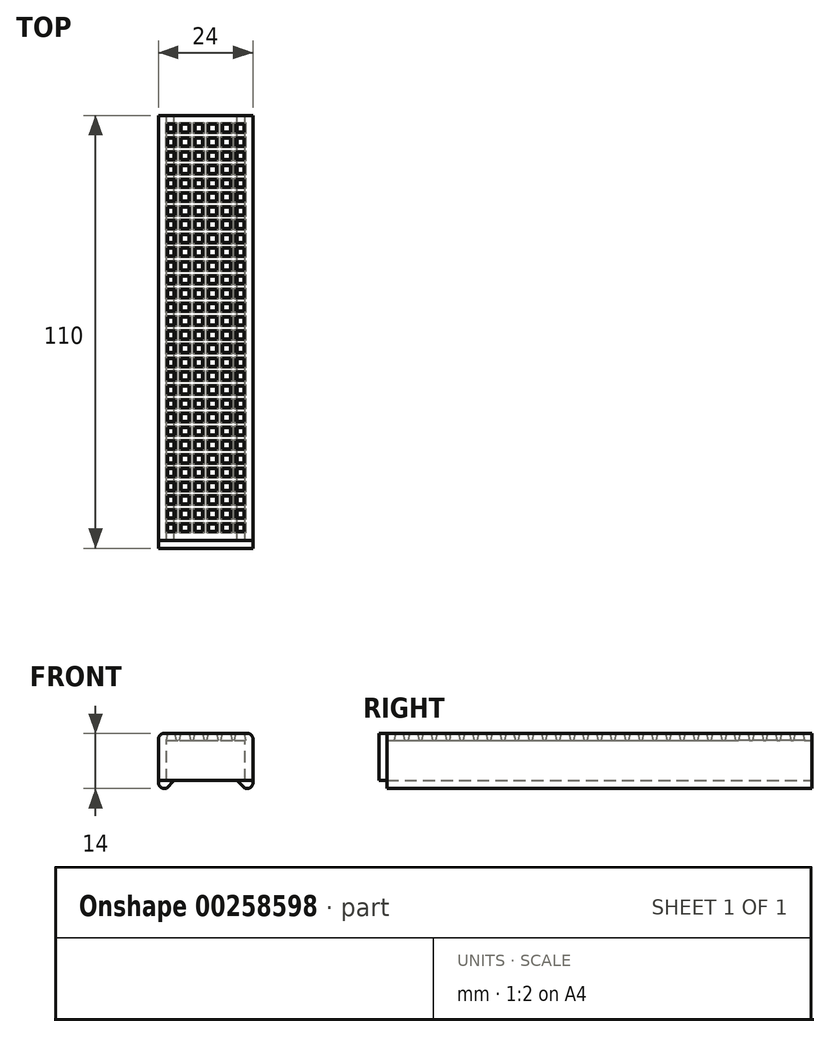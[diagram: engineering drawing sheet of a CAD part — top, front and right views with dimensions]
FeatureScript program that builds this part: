
annotation { "Feature Type Name" : "Feature", "Feature Type Description" : "" }
export const myFeature = defineFeature(function(context is Context, id is Id, definition is map)
    precondition{}
    {
        {
            var Q0;
            Q0=qCreatedBy(makeId("Front.planeOp"),FACE);
            var sketch = newSketch(context, id + "F0", { "sketchPlane" : qUnion([Q0])});
            skLineSegment(sketch, "E0.bottom", {"start": v(-10, -5.1) * mm, "end": v(-8, -5.1) * mm});
            skLineSegment(sketch, "E0.left", {"start": v(-10, -5.1) * mm, "end": v(-10, 5.1) * mm});
            skLineSegment(sketch, "E0.right", {"start": v(10, -5.1) * mm, "end": v(10, 5.1) * mm});
            skPoint(sketch, "E0.middle", {"position": v(0, 0) * mm});
            skPoint(sketch, "E1", {"position": v(-8, -5.1) * mm});
            skPoint(sketch, "E2.MirrorP", {"position": v(8, -5.1) * mm});
            skLineSegment(sketch, "E3", {"start": v(-8, -5.1) * mm, "end": v(-10, -7.1) * mm});
            skLineSegment(sketch, "E4", {"start": v(8, -5.1) * mm, "end": v(10, -7.1) * mm});
            skLineSegment(sketch, "E5", {"start": v(-12, -7.1) * mm, "end": v(-10, -7.1) * mm});
            skLineSegment(sketch, "E6.trimOffspring", {"start": v(10, -7.1) * mm, "end": v(12, -7.1) * mm});
            skLineSegment(sketch, "E7.trimOffspring", {"start": v(8, -5.1) * mm, "end": v(10, -5.1) * mm});
            skLineSegment(sketch, "E8", {"start": v(-10, 5.1) * mm, "end": v(10, 5.1) * mm});
            skLineSegment(sketch, "E9", {"start": v(-12, 6.9) * mm, "end": v(12, 6.9) * mm});
            skLineSegment(sketch, "E10", {"start": v(-12, -7.1) * mm, "end": v(-12, 6.9) * mm});
            skLineSegment(sketch, "E11", {"start": v(12, -7.1) * mm, "end": v(12, 6.9) * mm});
            skSolve(sketch);
        }
        {
            var Q0;
            Q0 = qSketchRegion(id + "F0", true);
            extrude(context, id + "F1", {"entities" : qUnion([Q0]), "depth" : 108 * mm});
        }
        {
            var Q0;
            Q0=makeQuery(id+"F1.opExtrude","SWEPT_FACE",FACE,{"disambiguationData":[OSD([sQuery(id+"F0.wireOp",EDGE,"E9")])]});
            var sketch = newSketch(context, id + "F2", { "sketchPlane" : qUnion([Q0])});
            skLineSegment(sketch, "E12.bottom", {"start": v(-9.75, -105.75) * mm, "end": v(-7.75, -105.75) * mm});
            skLineSegment(sketch, "E12.top", {"start": v(-9.75, -103.75) * mm, "end": v(-7.75, -103.75) * mm});
            skLineSegment(sketch, "E12.left", {"start": v(-9.75, -105.75) * mm, "end": v(-9.75, -103.75) * mm});
            skLineSegment(sketch, "E12.right", {"start": v(-7.75, -105.75) * mm, "end": v(-7.75, -103.75) * mm});
            skLineSegment(sketch, "E13.0.1.0", {"start": v(-7.75, -102.25) * mm, "end": v(-7.75, -100.25) * mm});
            skLineSegment(sketch, "E13.0.1.1", {"start": v(-9.75, -102.25) * mm, "end": v(-9.75, -100.25) * mm});
            skLineSegment(sketch, "E13.0.1.2", {"start": v(-9.75, -100.25) * mm, "end": v(-7.75, -100.25) * mm});
            skLineSegment(sketch, "E13.0.1.3", {"start": v(-9.75, -102.25) * mm, "end": v(-7.75, -102.25) * mm});
            skLineSegment(sketch, "E13.0.2.0", {"start": v(-7.75, -98.75) * mm, "end": v(-7.75, -96.75) * mm});
            skLineSegment(sketch, "E13.0.2.1", {"start": v(-9.75, -98.75) * mm, "end": v(-9.75, -96.75) * mm});
            skLineSegment(sketch, "E13.0.2.2", {"start": v(-9.75, -96.75) * mm, "end": v(-7.75, -96.75) * mm});
            skLineSegment(sketch, "E13.0.2.3", {"start": v(-9.75, -98.75) * mm, "end": v(-7.75, -98.75) * mm});
            skLineSegment(sketch, "E13.0.3.0", {"start": v(-7.75, -95.25) * mm, "end": v(-7.75, -93.25) * mm});
            skLineSegment(sketch, "E13.0.3.1", {"start": v(-9.75, -95.25) * mm, "end": v(-9.75, -93.25) * mm});
            skLineSegment(sketch, "E13.0.3.2", {"start": v(-9.75, -93.25) * mm, "end": v(-7.75, -93.25) * mm});
            skLineSegment(sketch, "E13.0.3.3", {"start": v(-9.75, -95.25) * mm, "end": v(-7.75, -95.25) * mm});
            skLineSegment(sketch, "E13.0.4.0", {"start": v(-7.75, -91.75) * mm, "end": v(-7.75, -89.75) * mm});
            skLineSegment(sketch, "E13.0.4.1", {"start": v(-9.75, -91.75) * mm, "end": v(-9.75, -89.75) * mm});
            skLineSegment(sketch, "E13.0.4.2", {"start": v(-9.75, -89.75) * mm, "end": v(-7.75, -89.75) * mm});
            skLineSegment(sketch, "E13.0.4.3", {"start": v(-9.75, -91.75) * mm, "end": v(-7.75, -91.75) * mm});
            skLineSegment(sketch, "E13.0.5.0", {"start": v(-7.75, -88.25) * mm, "end": v(-7.75, -86.25) * mm});
            skLineSegment(sketch, "E13.0.5.1", {"start": v(-9.75, -88.25) * mm, "end": v(-9.75, -86.25) * mm});
            skLineSegment(sketch, "E13.0.5.2", {"start": v(-9.75, -86.25) * mm, "end": v(-7.75, -86.25) * mm});
            skLineSegment(sketch, "E13.0.5.3", {"start": v(-9.75, -88.25) * mm, "end": v(-7.75, -88.25) * mm});
            skLineSegment(sketch, "E13.0.6.0", {"start": v(-7.75, -84.75) * mm, "end": v(-7.75, -82.75) * mm});
            skLineSegment(sketch, "E13.0.6.1", {"start": v(-9.75, -84.75) * mm, "end": v(-9.75, -82.75) * mm});
            skLineSegment(sketch, "E13.0.6.2", {"start": v(-9.75, -82.75) * mm, "end": v(-7.75, -82.75) * mm});
            skLineSegment(sketch, "E13.0.6.3", {"start": v(-9.75, -84.75) * mm, "end": v(-7.75, -84.75) * mm});
            skLineSegment(sketch, "E13.0.7.0", {"start": v(-7.75, -81.25) * mm, "end": v(-7.75, -79.25) * mm});
            skLineSegment(sketch, "E13.0.7.1", {"start": v(-9.75, -81.25) * mm, "end": v(-9.75, -79.25) * mm});
            skLineSegment(sketch, "E13.0.7.2", {"start": v(-9.75, -79.25) * mm, "end": v(-7.75, -79.25) * mm});
            skLineSegment(sketch, "E13.0.7.3", {"start": v(-9.75, -81.25) * mm, "end": v(-7.75, -81.25) * mm});
            skLineSegment(sketch, "E13.0.8.0", {"start": v(-7.75, -77.75) * mm, "end": v(-7.75, -75.75) * mm});
            skLineSegment(sketch, "E13.0.8.1", {"start": v(-9.75, -77.75) * mm, "end": v(-9.75, -75.75) * mm});
            skLineSegment(sketch, "E13.0.8.2", {"start": v(-9.75, -75.75) * mm, "end": v(-7.75, -75.75) * mm});
            skLineSegment(sketch, "E13.0.8.3", {"start": v(-9.75, -77.75) * mm, "end": v(-7.75, -77.75) * mm});
            skLineSegment(sketch, "E13.0.9.0", {"start": v(-7.75, -74.25) * mm, "end": v(-7.75, -72.25) * mm});
            skLineSegment(sketch, "E13.0.9.1", {"start": v(-9.75, -74.25) * mm, "end": v(-9.75, -72.25) * mm});
            skLineSegment(sketch, "E13.0.9.2", {"start": v(-9.75, -72.25) * mm, "end": v(-7.75, -72.25) * mm});
            skLineSegment(sketch, "E13.0.9.3", {"start": v(-9.75, -74.25) * mm, "end": v(-7.75, -74.25) * mm});
            skLineSegment(sketch, "E13.0.10.0", {"start": v(-7.75, -70.75) * mm, "end": v(-7.75, -68.75) * mm});
            skLineSegment(sketch, "E13.0.10.1", {"start": v(-9.75, -70.75) * mm, "end": v(-9.75, -68.75) * mm});
            skLineSegment(sketch, "E13.0.10.2", {"start": v(-9.75, -68.75) * mm, "end": v(-7.75, -68.75) * mm});
            skLineSegment(sketch, "E13.0.10.3", {"start": v(-9.75, -70.75) * mm, "end": v(-7.75, -70.75) * mm});
            skLineSegment(sketch, "E13.0.11.0", {"start": v(-7.75, -67.25) * mm, "end": v(-7.75, -65.25) * mm});
            skLineSegment(sketch, "E13.0.11.1", {"start": v(-9.75, -67.25) * mm, "end": v(-9.75, -65.25) * mm});
            skLineSegment(sketch, "E13.0.11.2", {"start": v(-9.75, -65.25) * mm, "end": v(-7.75, -65.25) * mm});
            skLineSegment(sketch, "E13.0.11.3", {"start": v(-9.75, -67.25) * mm, "end": v(-7.75, -67.25) * mm});
            skLineSegment(sketch, "E13.0.12.0", {"start": v(-7.75, -63.75) * mm, "end": v(-7.75, -61.75) * mm});
            skLineSegment(sketch, "E13.0.12.1", {"start": v(-9.75, -63.75) * mm, "end": v(-9.75, -61.75) * mm});
            skLineSegment(sketch, "E13.0.12.2", {"start": v(-9.75, -61.75) * mm, "end": v(-7.75, -61.75) * mm});
            skLineSegment(sketch, "E13.0.12.3", {"start": v(-9.75, -63.75) * mm, "end": v(-7.75, -63.75) * mm});
            skLineSegment(sketch, "E13.0.13.0", {"start": v(-7.75, -60.25) * mm, "end": v(-7.75, -58.25) * mm});
            skLineSegment(sketch, "E13.0.13.1", {"start": v(-9.75, -60.25) * mm, "end": v(-9.75, -58.25) * mm});
            skLineSegment(sketch, "E13.0.13.2", {"start": v(-9.75, -58.25) * mm, "end": v(-7.75, -58.25) * mm});
            skLineSegment(sketch, "E13.0.13.3", {"start": v(-9.75, -60.25) * mm, "end": v(-7.75, -60.25) * mm});
            skLineSegment(sketch, "E13.0.14.0", {"start": v(-7.75, -56.75) * mm, "end": v(-7.75, -54.75) * mm});
            skLineSegment(sketch, "E13.0.14.1", {"start": v(-9.75, -56.75) * mm, "end": v(-9.75, -54.75) * mm});
            skLineSegment(sketch, "E13.0.14.2", {"start": v(-9.75, -54.75) * mm, "end": v(-7.75, -54.75) * mm});
            skLineSegment(sketch, "E13.0.14.3", {"start": v(-9.75, -56.75) * mm, "end": v(-7.75, -56.75) * mm});
            skLineSegment(sketch, "E13.0.15.0", {"start": v(-7.75, -53.25) * mm, "end": v(-7.75, -51.25) * mm});
            skLineSegment(sketch, "E13.0.15.1", {"start": v(-9.75, -53.25) * mm, "end": v(-9.75, -51.25) * mm});
            skLineSegment(sketch, "E13.0.15.2", {"start": v(-9.75, -51.25) * mm, "end": v(-7.75, -51.25) * mm});
            skLineSegment(sketch, "E13.0.15.3", {"start": v(-9.75, -53.25) * mm, "end": v(-7.75, -53.25) * mm});
            skLineSegment(sketch, "E13.0.16.0", {"start": v(-7.75, -49.75) * mm, "end": v(-7.75, -47.75) * mm});
            skLineSegment(sketch, "E13.0.16.1", {"start": v(-9.75, -49.75) * mm, "end": v(-9.75, -47.75) * mm});
            skLineSegment(sketch, "E13.0.16.2", {"start": v(-9.75, -47.75) * mm, "end": v(-7.75, -47.75) * mm});
            skLineSegment(sketch, "E13.0.16.3", {"start": v(-9.75, -49.75) * mm, "end": v(-7.75, -49.75) * mm});
            skLineSegment(sketch, "E13.0.17.0", {"start": v(-7.75, -46.25) * mm, "end": v(-7.75, -44.25) * mm});
            skLineSegment(sketch, "E13.0.17.1", {"start": v(-9.75, -46.25) * mm, "end": v(-9.75, -44.25) * mm});
            skLineSegment(sketch, "E13.0.17.2", {"start": v(-9.75, -44.25) * mm, "end": v(-7.75, -44.25) * mm});
            skLineSegment(sketch, "E13.0.17.3", {"start": v(-9.75, -46.25) * mm, "end": v(-7.75, -46.25) * mm});
            skLineSegment(sketch, "E13.0.18.0", {"start": v(-7.75, -42.75) * mm, "end": v(-7.75, -40.75) * mm});
            skLineSegment(sketch, "E13.0.18.1", {"start": v(-9.75, -42.75) * mm, "end": v(-9.75, -40.75) * mm});
            skLineSegment(sketch, "E13.0.18.2", {"start": v(-9.75, -40.75) * mm, "end": v(-7.75, -40.75) * mm});
            skLineSegment(sketch, "E13.0.18.3", {"start": v(-9.75, -42.75) * mm, "end": v(-7.75, -42.75) * mm});
            skLineSegment(sketch, "E13.0.19.0", {"start": v(-7.75, -39.25) * mm, "end": v(-7.75, -37.25) * mm});
            skLineSegment(sketch, "E13.0.19.1", {"start": v(-9.75, -39.25) * mm, "end": v(-9.75, -37.25) * mm});
            skLineSegment(sketch, "E13.0.19.2", {"start": v(-9.75, -37.25) * mm, "end": v(-7.75, -37.25) * mm});
            skLineSegment(sketch, "E13.0.19.3", {"start": v(-9.75, -39.25) * mm, "end": v(-7.75, -39.25) * mm});
            skLineSegment(sketch, "E13.0.20.0", {"start": v(-7.75, -35.75) * mm, "end": v(-7.75, -33.75) * mm});
            skLineSegment(sketch, "E13.0.20.1", {"start": v(-9.75, -35.75) * mm, "end": v(-9.75, -33.75) * mm});
            skLineSegment(sketch, "E13.0.20.2", {"start": v(-9.75, -33.75) * mm, "end": v(-7.75, -33.75) * mm});
            skLineSegment(sketch, "E13.0.20.3", {"start": v(-9.75, -35.75) * mm, "end": v(-7.75, -35.75) * mm});
            skLineSegment(sketch, "E13.0.21.0", {"start": v(-7.75, -32.25) * mm, "end": v(-7.75, -30.25) * mm});
            skLineSegment(sketch, "E13.0.21.1", {"start": v(-9.75, -32.25) * mm, "end": v(-9.75, -30.25) * mm});
            skLineSegment(sketch, "E13.0.21.2", {"start": v(-9.75, -30.25) * mm, "end": v(-7.75, -30.25) * mm});
            skLineSegment(sketch, "E13.0.21.3", {"start": v(-9.75, -32.25) * mm, "end": v(-7.75, -32.25) * mm});
            skLineSegment(sketch, "E13.0.22.0", {"start": v(-7.75, -28.75) * mm, "end": v(-7.75, -26.75) * mm});
            skLineSegment(sketch, "E13.0.22.1", {"start": v(-9.75, -28.75) * mm, "end": v(-9.75, -26.75) * mm});
            skLineSegment(sketch, "E13.0.22.2", {"start": v(-9.75, -26.75) * mm, "end": v(-7.75, -26.75) * mm});
            skLineSegment(sketch, "E13.0.22.3", {"start": v(-9.75, -28.75) * mm, "end": v(-7.75, -28.75) * mm});
            skLineSegment(sketch, "E13.0.23.0", {"start": v(-7.75, -25.25) * mm, "end": v(-7.75, -23.25) * mm});
            skLineSegment(sketch, "E13.0.23.1", {"start": v(-9.75, -25.25) * mm, "end": v(-9.75, -23.25) * mm});
            skLineSegment(sketch, "E13.0.23.2", {"start": v(-9.75, -23.25) * mm, "end": v(-7.75, -23.25) * mm});
            skLineSegment(sketch, "E13.0.23.3", {"start": v(-9.75, -25.25) * mm, "end": v(-7.75, -25.25) * mm});
            skLineSegment(sketch, "E13.0.24.0", {"start": v(-7.75, -21.75) * mm, "end": v(-7.75, -19.75) * mm});
            skLineSegment(sketch, "E13.0.24.1", {"start": v(-9.75, -21.75) * mm, "end": v(-9.75, -19.75) * mm});
            skLineSegment(sketch, "E13.0.24.2", {"start": v(-9.75, -19.75) * mm, "end": v(-7.75, -19.75) * mm});
            skLineSegment(sketch, "E13.0.24.3", {"start": v(-9.75, -21.75) * mm, "end": v(-7.75, -21.75) * mm});
            skLineSegment(sketch, "E13.1.0.0", {"start": v(-4.25, -105.75) * mm, "end": v(-4.25, -103.75) * mm});
            skLineSegment(sketch, "E13.1.0.1", {"start": v(-6.25, -105.75) * mm, "end": v(-6.25, -103.75) * mm});
            skLineSegment(sketch, "E13.1.0.2", {"start": v(-6.25, -103.75) * mm, "end": v(-4.25, -103.75) * mm});
            skLineSegment(sketch, "E13.1.0.3", {"start": v(-6.25, -105.75) * mm, "end": v(-4.25, -105.75) * mm});
            skLineSegment(sketch, "E13.1.1.0", {"start": v(-4.25, -102.25) * mm, "end": v(-4.25, -100.25) * mm});
            skLineSegment(sketch, "E13.1.1.1", {"start": v(-6.25, -102.25) * mm, "end": v(-6.25, -100.25) * mm});
            skLineSegment(sketch, "E13.1.1.2", {"start": v(-6.25, -100.25) * mm, "end": v(-4.25, -100.25) * mm});
            skLineSegment(sketch, "E13.1.1.3", {"start": v(-6.25, -102.25) * mm, "end": v(-4.25, -102.25) * mm});
            skLineSegment(sketch, "E13.1.2.0", {"start": v(-4.25, -98.75) * mm, "end": v(-4.25, -96.75) * mm});
            skLineSegment(sketch, "E13.1.2.1", {"start": v(-6.25, -98.75) * mm, "end": v(-6.25, -96.75) * mm});
            skLineSegment(sketch, "E13.1.2.2", {"start": v(-6.25, -96.75) * mm, "end": v(-4.25, -96.75) * mm});
            skLineSegment(sketch, "E13.1.2.3", {"start": v(-6.25, -98.75) * mm, "end": v(-4.25, -98.75) * mm});
            skLineSegment(sketch, "E13.1.3.0", {"start": v(-4.25, -95.25) * mm, "end": v(-4.25, -93.25) * mm});
            skLineSegment(sketch, "E13.1.3.1", {"start": v(-6.25, -95.25) * mm, "end": v(-6.25, -93.25) * mm});
            skLineSegment(sketch, "E13.1.3.2", {"start": v(-6.25, -93.25) * mm, "end": v(-4.25, -93.25) * mm});
            skLineSegment(sketch, "E13.1.3.3", {"start": v(-6.25, -95.25) * mm, "end": v(-4.25, -95.25) * mm});
            skLineSegment(sketch, "E13.1.4.0", {"start": v(-4.25, -91.75) * mm, "end": v(-4.25, -89.75) * mm});
            skLineSegment(sketch, "E13.1.4.1", {"start": v(-6.25, -91.75) * mm, "end": v(-6.25, -89.75) * mm});
            skLineSegment(sketch, "E13.1.4.2", {"start": v(-6.25, -89.75) * mm, "end": v(-4.25, -89.75) * mm});
            skLineSegment(sketch, "E13.1.4.3", {"start": v(-6.25, -91.75) * mm, "end": v(-4.25, -91.75) * mm});
            skLineSegment(sketch, "E13.1.5.0", {"start": v(-4.25, -88.25) * mm, "end": v(-4.25, -86.25) * mm});
            skLineSegment(sketch, "E13.1.5.1", {"start": v(-6.25, -88.25) * mm, "end": v(-6.25, -86.25) * mm});
            skLineSegment(sketch, "E13.1.5.2", {"start": v(-6.25, -86.25) * mm, "end": v(-4.25, -86.25) * mm});
            skLineSegment(sketch, "E13.1.5.3", {"start": v(-6.25, -88.25) * mm, "end": v(-4.25, -88.25) * mm});
            skLineSegment(sketch, "E13.1.6.0", {"start": v(-4.25, -84.75) * mm, "end": v(-4.25, -82.75) * mm});
            skLineSegment(sketch, "E13.1.6.1", {"start": v(-6.25, -84.75) * mm, "end": v(-6.25, -82.75) * mm});
            skLineSegment(sketch, "E13.1.6.2", {"start": v(-6.25, -82.75) * mm, "end": v(-4.25, -82.75) * mm});
            skLineSegment(sketch, "E13.1.6.3", {"start": v(-6.25, -84.75) * mm, "end": v(-4.25, -84.75) * mm});
            skLineSegment(sketch, "E13.1.7.0", {"start": v(-4.25, -81.25) * mm, "end": v(-4.25, -79.25) * mm});
            skLineSegment(sketch, "E13.1.7.1", {"start": v(-6.25, -81.25) * mm, "end": v(-6.25, -79.25) * mm});
            skLineSegment(sketch, "E13.1.7.2", {"start": v(-6.25, -79.25) * mm, "end": v(-4.25, -79.25) * mm});
            skLineSegment(sketch, "E13.1.7.3", {"start": v(-6.25, -81.25) * mm, "end": v(-4.25, -81.25) * mm});
            skLineSegment(sketch, "E13.1.8.0", {"start": v(-4.25, -77.75) * mm, "end": v(-4.25, -75.75) * mm});
            skLineSegment(sketch, "E13.1.8.1", {"start": v(-6.25, -77.75) * mm, "end": v(-6.25, -75.75) * mm});
            skLineSegment(sketch, "E13.1.8.2", {"start": v(-6.25, -75.75) * mm, "end": v(-4.25, -75.75) * mm});
            skLineSegment(sketch, "E13.1.8.3", {"start": v(-6.25, -77.75) * mm, "end": v(-4.25, -77.75) * mm});
            skLineSegment(sketch, "E13.1.9.0", {"start": v(-4.25, -74.25) * mm, "end": v(-4.25, -72.25) * mm});
            skLineSegment(sketch, "E13.1.9.1", {"start": v(-6.25, -74.25) * mm, "end": v(-6.25, -72.25) * mm});
            skLineSegment(sketch, "E13.1.9.2", {"start": v(-6.25, -72.25) * mm, "end": v(-4.25, -72.25) * mm});
            skLineSegment(sketch, "E13.1.9.3", {"start": v(-6.25, -74.25) * mm, "end": v(-4.25, -74.25) * mm});
            skLineSegment(sketch, "E13.1.10.0", {"start": v(-4.25, -70.75) * mm, "end": v(-4.25, -68.75) * mm});
            skLineSegment(sketch, "E13.1.10.1", {"start": v(-6.25, -70.75) * mm, "end": v(-6.25, -68.75) * mm});
            skLineSegment(sketch, "E13.1.10.2", {"start": v(-6.25, -68.75) * mm, "end": v(-4.25, -68.75) * mm});
            skLineSegment(sketch, "E13.1.10.3", {"start": v(-6.25, -70.75) * mm, "end": v(-4.25, -70.75) * mm});
            skLineSegment(sketch, "E13.1.11.0", {"start": v(-4.25, -67.25) * mm, "end": v(-4.25, -65.25) * mm});
            skLineSegment(sketch, "E13.1.11.1", {"start": v(-6.25, -67.25) * mm, "end": v(-6.25, -65.25) * mm});
            skLineSegment(sketch, "E13.1.11.2", {"start": v(-6.25, -65.25) * mm, "end": v(-4.25, -65.25) * mm});
            skLineSegment(sketch, "E13.1.11.3", {"start": v(-6.25, -67.25) * mm, "end": v(-4.25, -67.25) * mm});
            skLineSegment(sketch, "E13.1.12.0", {"start": v(-4.25, -63.75) * mm, "end": v(-4.25, -61.75) * mm});
            skLineSegment(sketch, "E13.1.12.1", {"start": v(-6.25, -63.75) * mm, "end": v(-6.25, -61.75) * mm});
            skLineSegment(sketch, "E13.1.12.2", {"start": v(-6.25, -61.75) * mm, "end": v(-4.25, -61.75) * mm});
            skLineSegment(sketch, "E13.1.12.3", {"start": v(-6.25, -63.75) * mm, "end": v(-4.25, -63.75) * mm});
            skLineSegment(sketch, "E13.1.13.0", {"start": v(-4.25, -60.25) * mm, "end": v(-4.25, -58.25) * mm});
            skLineSegment(sketch, "E13.1.13.1", {"start": v(-6.25, -60.25) * mm, "end": v(-6.25, -58.25) * mm});
            skLineSegment(sketch, "E13.1.13.2", {"start": v(-6.25, -58.25) * mm, "end": v(-4.25, -58.25) * mm});
            skLineSegment(sketch, "E13.1.13.3", {"start": v(-6.25, -60.25) * mm, "end": v(-4.25, -60.25) * mm});
            skLineSegment(sketch, "E13.1.14.0", {"start": v(-4.25, -56.75) * mm, "end": v(-4.25, -54.75) * mm});
            skLineSegment(sketch, "E13.1.14.1", {"start": v(-6.25, -56.75) * mm, "end": v(-6.25, -54.75) * mm});
            skLineSegment(sketch, "E13.1.14.2", {"start": v(-6.25, -54.75) * mm, "end": v(-4.25, -54.75) * mm});
            skLineSegment(sketch, "E13.1.14.3", {"start": v(-6.25, -56.75) * mm, "end": v(-4.25, -56.75) * mm});
            skLineSegment(sketch, "E13.1.15.0", {"start": v(-4.25, -53.25) * mm, "end": v(-4.25, -51.25) * mm});
            skLineSegment(sketch, "E13.1.15.1", {"start": v(-6.25, -53.25) * mm, "end": v(-6.25, -51.25) * mm});
            skLineSegment(sketch, "E13.1.15.2", {"start": v(-6.25, -51.25) * mm, "end": v(-4.25, -51.25) * mm});
            skLineSegment(sketch, "E13.1.15.3", {"start": v(-6.25, -53.25) * mm, "end": v(-4.25, -53.25) * mm});
            skLineSegment(sketch, "E13.1.16.0", {"start": v(-4.25, -49.75) * mm, "end": v(-4.25, -47.75) * mm});
            skLineSegment(sketch, "E13.1.16.1", {"start": v(-6.25, -49.75) * mm, "end": v(-6.25, -47.75) * mm});
            skLineSegment(sketch, "E13.1.16.2", {"start": v(-6.25, -47.75) * mm, "end": v(-4.25, -47.75) * mm});
            skLineSegment(sketch, "E13.1.16.3", {"start": v(-6.25, -49.75) * mm, "end": v(-4.25, -49.75) * mm});
            skLineSegment(sketch, "E13.1.17.0", {"start": v(-4.25, -46.25) * mm, "end": v(-4.25, -44.25) * mm});
            skLineSegment(sketch, "E13.1.17.1", {"start": v(-6.25, -46.25) * mm, "end": v(-6.25, -44.25) * mm});
            skLineSegment(sketch, "E13.1.17.2", {"start": v(-6.25, -44.25) * mm, "end": v(-4.25, -44.25) * mm});
            skLineSegment(sketch, "E13.1.17.3", {"start": v(-6.25, -46.25) * mm, "end": v(-4.25, -46.25) * mm});
            skLineSegment(sketch, "E13.1.18.0", {"start": v(-4.25, -42.75) * mm, "end": v(-4.25, -40.75) * mm});
            skLineSegment(sketch, "E13.1.18.1", {"start": v(-6.25, -42.75) * mm, "end": v(-6.25, -40.75) * mm});
            skLineSegment(sketch, "E13.1.18.2", {"start": v(-6.25, -40.75) * mm, "end": v(-4.25, -40.75) * mm});
            skLineSegment(sketch, "E13.1.18.3", {"start": v(-6.25, -42.75) * mm, "end": v(-4.25, -42.75) * mm});
            skLineSegment(sketch, "E13.1.19.0", {"start": v(-4.25, -39.25) * mm, "end": v(-4.25, -37.25) * mm});
            skLineSegment(sketch, "E13.1.19.1", {"start": v(-6.25, -39.25) * mm, "end": v(-6.25, -37.25) * mm});
            skLineSegment(sketch, "E13.1.19.2", {"start": v(-6.25, -37.25) * mm, "end": v(-4.25, -37.25) * mm});
            skLineSegment(sketch, "E13.1.19.3", {"start": v(-6.25, -39.25) * mm, "end": v(-4.25, -39.25) * mm});
            skLineSegment(sketch, "E13.1.20.0", {"start": v(-4.25, -35.75) * mm, "end": v(-4.25, -33.75) * mm});
            skLineSegment(sketch, "E13.1.20.1", {"start": v(-6.25, -35.75) * mm, "end": v(-6.25, -33.75) * mm});
            skLineSegment(sketch, "E13.1.20.2", {"start": v(-6.25, -33.75) * mm, "end": v(-4.25, -33.75) * mm});
            skLineSegment(sketch, "E13.1.20.3", {"start": v(-6.25, -35.75) * mm, "end": v(-4.25, -35.75) * mm});
            skLineSegment(sketch, "E13.1.21.0", {"start": v(-4.25, -32.25) * mm, "end": v(-4.25, -30.25) * mm});
            skLineSegment(sketch, "E13.1.21.1", {"start": v(-6.25, -32.25) * mm, "end": v(-6.25, -30.25) * mm});
            skLineSegment(sketch, "E13.1.21.2", {"start": v(-6.25, -30.25) * mm, "end": v(-4.25, -30.25) * mm});
            skLineSegment(sketch, "E13.1.21.3", {"start": v(-6.25, -32.25) * mm, "end": v(-4.25, -32.25) * mm});
            skLineSegment(sketch, "E13.1.22.0", {"start": v(-4.25, -28.75) * mm, "end": v(-4.25, -26.75) * mm});
            skLineSegment(sketch, "E13.1.22.1", {"start": v(-6.25, -28.75) * mm, "end": v(-6.25, -26.75) * mm});
            skLineSegment(sketch, "E13.1.22.2", {"start": v(-6.25, -26.75) * mm, "end": v(-4.25, -26.75) * mm});
            skLineSegment(sketch, "E13.1.22.3", {"start": v(-6.25, -28.75) * mm, "end": v(-4.25, -28.75) * mm});
            skLineSegment(sketch, "E13.1.23.0", {"start": v(-4.25, -25.25) * mm, "end": v(-4.25, -23.25) * mm});
            skLineSegment(sketch, "E13.1.23.1", {"start": v(-6.25, -25.25) * mm, "end": v(-6.25, -23.25) * mm});
            skLineSegment(sketch, "E13.1.23.2", {"start": v(-6.25, -23.25) * mm, "end": v(-4.25, -23.25) * mm});
            skLineSegment(sketch, "E13.1.23.3", {"start": v(-6.25, -25.25) * mm, "end": v(-4.25, -25.25) * mm});
            skLineSegment(sketch, "E13.1.24.0", {"start": v(-4.25, -21.75) * mm, "end": v(-4.25, -19.75) * mm});
            skLineSegment(sketch, "E13.1.24.1", {"start": v(-6.25, -21.75) * mm, "end": v(-6.25, -19.75) * mm});
            skLineSegment(sketch, "E13.1.24.2", {"start": v(-6.25, -19.75) * mm, "end": v(-4.25, -19.75) * mm});
            skLineSegment(sketch, "E13.1.24.3", {"start": v(-6.25, -21.75) * mm, "end": v(-4.25, -21.75) * mm});
            skLineSegment(sketch, "E13.2.0.0", {"start": v(-0.75, -105.75) * mm, "end": v(-0.75, -103.75) * mm});
            skLineSegment(sketch, "E13.2.0.1", {"start": v(-2.75, -105.75) * mm, "end": v(-2.75, -103.75) * mm});
            skLineSegment(sketch, "E13.2.0.2", {"start": v(-2.75, -103.75) * mm, "end": v(-0.75, -103.75) * mm});
            skLineSegment(sketch, "E13.2.0.3", {"start": v(-2.75, -105.75) * mm, "end": v(-0.75, -105.75) * mm});
            skLineSegment(sketch, "E13.2.1.0", {"start": v(-0.75, -102.25) * mm, "end": v(-0.75, -100.25) * mm});
            skLineSegment(sketch, "E13.2.1.1", {"start": v(-2.75, -102.25) * mm, "end": v(-2.75, -100.25) * mm});
            skLineSegment(sketch, "E13.2.1.2", {"start": v(-2.75, -100.25) * mm, "end": v(-0.75, -100.25) * mm});
            skLineSegment(sketch, "E13.2.1.3", {"start": v(-2.75, -102.25) * mm, "end": v(-0.75, -102.25) * mm});
            skLineSegment(sketch, "E13.2.2.0", {"start": v(-0.75, -98.75) * mm, "end": v(-0.75, -96.75) * mm});
            skLineSegment(sketch, "E13.2.2.1", {"start": v(-2.75, -98.75) * mm, "end": v(-2.75, -96.75) * mm});
            skLineSegment(sketch, "E13.2.2.2", {"start": v(-2.75, -96.75) * mm, "end": v(-0.75, -96.75) * mm});
            skLineSegment(sketch, "E13.2.2.3", {"start": v(-2.75, -98.75) * mm, "end": v(-0.75, -98.75) * mm});
            skLineSegment(sketch, "E13.2.3.0", {"start": v(-0.75, -95.25) * mm, "end": v(-0.75, -93.25) * mm});
            skLineSegment(sketch, "E13.2.3.1", {"start": v(-2.75, -95.25) * mm, "end": v(-2.75, -93.25) * mm});
            skLineSegment(sketch, "E13.2.3.2", {"start": v(-2.75, -93.25) * mm, "end": v(-0.75, -93.25) * mm});
            skLineSegment(sketch, "E13.2.3.3", {"start": v(-2.75, -95.25) * mm, "end": v(-0.75, -95.25) * mm});
            skLineSegment(sketch, "E13.2.4.0", {"start": v(-0.75, -91.75) * mm, "end": v(-0.75, -89.75) * mm});
            skLineSegment(sketch, "E13.2.4.1", {"start": v(-2.75, -91.75) * mm, "end": v(-2.75, -89.75) * mm});
            skLineSegment(sketch, "E13.2.4.2", {"start": v(-2.75, -89.75) * mm, "end": v(-0.75, -89.75) * mm});
            skLineSegment(sketch, "E13.2.4.3", {"start": v(-2.75, -91.75) * mm, "end": v(-0.75, -91.75) * mm});
            skLineSegment(sketch, "E13.2.5.0", {"start": v(-0.75, -88.25) * mm, "end": v(-0.75, -86.25) * mm});
            skLineSegment(sketch, "E13.2.5.1", {"start": v(-2.75, -88.25) * mm, "end": v(-2.75, -86.25) * mm});
            skLineSegment(sketch, "E13.2.5.2", {"start": v(-2.75, -86.25) * mm, "end": v(-0.75, -86.25) * mm});
            skLineSegment(sketch, "E13.2.5.3", {"start": v(-2.75, -88.25) * mm, "end": v(-0.75, -88.25) * mm});
            skLineSegment(sketch, "E13.2.6.0", {"start": v(-0.75, -84.75) * mm, "end": v(-0.75, -82.75) * mm});
            skLineSegment(sketch, "E13.2.6.1", {"start": v(-2.75, -84.75) * mm, "end": v(-2.75, -82.75) * mm});
            skLineSegment(sketch, "E13.2.6.2", {"start": v(-2.75, -82.75) * mm, "end": v(-0.75, -82.75) * mm});
            skLineSegment(sketch, "E13.2.6.3", {"start": v(-2.75, -84.75) * mm, "end": v(-0.75, -84.75) * mm});
            skLineSegment(sketch, "E13.2.7.0", {"start": v(-0.75, -81.25) * mm, "end": v(-0.75, -79.25) * mm});
            skLineSegment(sketch, "E13.2.7.1", {"start": v(-2.75, -81.25) * mm, "end": v(-2.75, -79.25) * mm});
            skLineSegment(sketch, "E13.2.7.2", {"start": v(-2.75, -79.25) * mm, "end": v(-0.75, -79.25) * mm});
            skLineSegment(sketch, "E13.2.7.3", {"start": v(-2.75, -81.25) * mm, "end": v(-0.75, -81.25) * mm});
            skLineSegment(sketch, "E13.2.8.0", {"start": v(-0.75, -77.75) * mm, "end": v(-0.75, -75.75) * mm});
            skLineSegment(sketch, "E13.2.8.1", {"start": v(-2.75, -77.75) * mm, "end": v(-2.75, -75.75) * mm});
            skLineSegment(sketch, "E13.2.8.2", {"start": v(-2.75, -75.75) * mm, "end": v(-0.75, -75.75) * mm});
            skLineSegment(sketch, "E13.2.8.3", {"start": v(-2.75, -77.75) * mm, "end": v(-0.75, -77.75) * mm});
            skLineSegment(sketch, "E13.2.9.0", {"start": v(-0.75, -74.25) * mm, "end": v(-0.75, -72.25) * mm});
            skLineSegment(sketch, "E13.2.9.1", {"start": v(-2.75, -74.25) * mm, "end": v(-2.75, -72.25) * mm});
            skLineSegment(sketch, "E13.2.9.2", {"start": v(-2.75, -72.25) * mm, "end": v(-0.75, -72.25) * mm});
            skLineSegment(sketch, "E13.2.9.3", {"start": v(-2.75, -74.25) * mm, "end": v(-0.75, -74.25) * mm});
            skLineSegment(sketch, "E13.2.10.0", {"start": v(-0.75, -70.75) * mm, "end": v(-0.75, -68.75) * mm});
            skLineSegment(sketch, "E13.2.10.1", {"start": v(-2.75, -70.75) * mm, "end": v(-2.75, -68.75) * mm});
            skLineSegment(sketch, "E13.2.10.2", {"start": v(-2.75, -68.75) * mm, "end": v(-0.75, -68.75) * mm});
            skLineSegment(sketch, "E13.2.10.3", {"start": v(-2.75, -70.75) * mm, "end": v(-0.75, -70.75) * mm});
            skLineSegment(sketch, "E13.2.11.0", {"start": v(-0.75, -67.25) * mm, "end": v(-0.75, -65.25) * mm});
            skLineSegment(sketch, "E13.2.11.1", {"start": v(-2.75, -67.25) * mm, "end": v(-2.75, -65.25) * mm});
            skLineSegment(sketch, "E13.2.11.2", {"start": v(-2.75, -65.25) * mm, "end": v(-0.75, -65.25) * mm});
            skLineSegment(sketch, "E13.2.11.3", {"start": v(-2.75, -67.25) * mm, "end": v(-0.75, -67.25) * mm});
            skLineSegment(sketch, "E13.2.12.0", {"start": v(-0.75, -63.75) * mm, "end": v(-0.75, -61.75) * mm});
            skLineSegment(sketch, "E13.2.12.1", {"start": v(-2.75, -63.75) * mm, "end": v(-2.75, -61.75) * mm});
            skLineSegment(sketch, "E13.2.12.2", {"start": v(-2.75, -61.75) * mm, "end": v(-0.75, -61.75) * mm});
            skLineSegment(sketch, "E13.2.12.3", {"start": v(-2.75, -63.75) * mm, "end": v(-0.75, -63.75) * mm});
            skLineSegment(sketch, "E13.2.13.0", {"start": v(-0.75, -60.25) * mm, "end": v(-0.75, -58.25) * mm});
            skLineSegment(sketch, "E13.2.13.1", {"start": v(-2.75, -60.25) * mm, "end": v(-2.75, -58.25) * mm});
            skLineSegment(sketch, "E13.2.13.2", {"start": v(-2.75, -58.25) * mm, "end": v(-0.75, -58.25) * mm});
            skLineSegment(sketch, "E13.2.13.3", {"start": v(-2.75, -60.25) * mm, "end": v(-0.75, -60.25) * mm});
            skLineSegment(sketch, "E13.2.14.0", {"start": v(-0.75, -56.75) * mm, "end": v(-0.75, -54.75) * mm});
            skLineSegment(sketch, "E13.2.14.1", {"start": v(-2.75, -56.75) * mm, "end": v(-2.75, -54.75) * mm});
            skLineSegment(sketch, "E13.2.14.2", {"start": v(-2.75, -54.75) * mm, "end": v(-0.75, -54.75) * mm});
            skLineSegment(sketch, "E13.2.14.3", {"start": v(-2.75, -56.75) * mm, "end": v(-0.75, -56.75) * mm});
            skLineSegment(sketch, "E13.2.15.0", {"start": v(-0.75, -53.25) * mm, "end": v(-0.75, -51.25) * mm});
            skLineSegment(sketch, "E13.2.15.1", {"start": v(-2.75, -53.25) * mm, "end": v(-2.75, -51.25) * mm});
            skLineSegment(sketch, "E13.2.15.2", {"start": v(-2.75, -51.25) * mm, "end": v(-0.75, -51.25) * mm});
            skLineSegment(sketch, "E13.2.15.3", {"start": v(-2.75, -53.25) * mm, "end": v(-0.75, -53.25) * mm});
            skLineSegment(sketch, "E13.2.16.0", {"start": v(-0.75, -49.75) * mm, "end": v(-0.75, -47.75) * mm});
            skLineSegment(sketch, "E13.2.16.1", {"start": v(-2.75, -49.75) * mm, "end": v(-2.75, -47.75) * mm});
            skLineSegment(sketch, "E13.2.16.2", {"start": v(-2.75, -47.75) * mm, "end": v(-0.75, -47.75) * mm});
            skLineSegment(sketch, "E13.2.16.3", {"start": v(-2.75, -49.75) * mm, "end": v(-0.75, -49.75) * mm});
            skLineSegment(sketch, "E13.2.17.0", {"start": v(-0.75, -46.25) * mm, "end": v(-0.75, -44.25) * mm});
            skLineSegment(sketch, "E13.2.17.1", {"start": v(-2.75, -46.25) * mm, "end": v(-2.75, -44.25) * mm});
            skLineSegment(sketch, "E13.2.17.2", {"start": v(-2.75, -44.25) * mm, "end": v(-0.75, -44.25) * mm});
            skLineSegment(sketch, "E13.2.17.3", {"start": v(-2.75, -46.25) * mm, "end": v(-0.75, -46.25) * mm});
            skLineSegment(sketch, "E13.2.18.0", {"start": v(-0.75, -42.75) * mm, "end": v(-0.75, -40.75) * mm});
            skLineSegment(sketch, "E13.2.18.1", {"start": v(-2.75, -42.75) * mm, "end": v(-2.75, -40.75) * mm});
            skLineSegment(sketch, "E13.2.18.2", {"start": v(-2.75, -40.75) * mm, "end": v(-0.75, -40.75) * mm});
            skLineSegment(sketch, "E13.2.18.3", {"start": v(-2.75, -42.75) * mm, "end": v(-0.75, -42.75) * mm});
            skLineSegment(sketch, "E13.2.19.0", {"start": v(-0.75, -39.25) * mm, "end": v(-0.75, -37.25) * mm});
            skLineSegment(sketch, "E13.2.19.1", {"start": v(-2.75, -39.25) * mm, "end": v(-2.75, -37.25) * mm});
            skLineSegment(sketch, "E13.2.19.2", {"start": v(-2.75, -37.25) * mm, "end": v(-0.75, -37.25) * mm});
            skLineSegment(sketch, "E13.2.19.3", {"start": v(-2.75, -39.25) * mm, "end": v(-0.75, -39.25) * mm});
            skLineSegment(sketch, "E13.2.20.0", {"start": v(-0.75, -35.75) * mm, "end": v(-0.75, -33.75) * mm});
            skLineSegment(sketch, "E13.2.20.1", {"start": v(-2.75, -35.75) * mm, "end": v(-2.75, -33.75) * mm});
            skLineSegment(sketch, "E13.2.20.2", {"start": v(-2.75, -33.75) * mm, "end": v(-0.75, -33.75) * mm});
            skLineSegment(sketch, "E13.2.20.3", {"start": v(-2.75, -35.75) * mm, "end": v(-0.75, -35.75) * mm});
            skLineSegment(sketch, "E13.2.21.0", {"start": v(-0.75, -32.25) * mm, "end": v(-0.75, -30.25) * mm});
            skLineSegment(sketch, "E13.2.21.1", {"start": v(-2.75, -32.25) * mm, "end": v(-2.75, -30.25) * mm});
            skLineSegment(sketch, "E13.2.21.2", {"start": v(-2.75, -30.25) * mm, "end": v(-0.75, -30.25) * mm});
            skLineSegment(sketch, "E13.2.21.3", {"start": v(-2.75, -32.25) * mm, "end": v(-0.75, -32.25) * mm});
            skLineSegment(sketch, "E13.2.22.0", {"start": v(-0.75, -28.75) * mm, "end": v(-0.75, -26.75) * mm});
            skLineSegment(sketch, "E13.2.22.1", {"start": v(-2.75, -28.75) * mm, "end": v(-2.75, -26.75) * mm});
            skLineSegment(sketch, "E13.2.22.2", {"start": v(-2.75, -26.75) * mm, "end": v(-0.75, -26.75) * mm});
            skLineSegment(sketch, "E13.2.22.3", {"start": v(-2.75, -28.75) * mm, "end": v(-0.75, -28.75) * mm});
            skLineSegment(sketch, "E13.2.23.0", {"start": v(-0.75, -25.25) * mm, "end": v(-0.75, -23.25) * mm});
            skLineSegment(sketch, "E13.2.23.1", {"start": v(-2.75, -25.25) * mm, "end": v(-2.75, -23.25) * mm});
            skLineSegment(sketch, "E13.2.23.2", {"start": v(-2.75, -23.25) * mm, "end": v(-0.75, -23.25) * mm});
            skLineSegment(sketch, "E13.2.23.3", {"start": v(-2.75, -25.25) * mm, "end": v(-0.75, -25.25) * mm});
            skLineSegment(sketch, "E13.2.24.0", {"start": v(-0.75, -21.75) * mm, "end": v(-0.75, -19.75) * mm});
            skLineSegment(sketch, "E13.2.24.1", {"start": v(-2.75, -21.75) * mm, "end": v(-2.75, -19.75) * mm});
            skLineSegment(sketch, "E13.2.24.2", {"start": v(-2.75, -19.75) * mm, "end": v(-0.75, -19.75) * mm});
            skLineSegment(sketch, "E13.2.24.3", {"start": v(-2.75, -21.75) * mm, "end": v(-0.75, -21.75) * mm});
            skLineSegment(sketch, "E13.3.0.0", {"start": v(2.75, -105.75) * mm, "end": v(2.75, -103.75) * mm});
            skLineSegment(sketch, "E13.3.0.1", {"start": v(0.75, -105.75) * mm, "end": v(0.75, -103.75) * mm});
            skLineSegment(sketch, "E13.3.0.2", {"start": v(0.75, -103.75) * mm, "end": v(2.75, -103.75) * mm});
            skLineSegment(sketch, "E13.3.0.3", {"start": v(0.75, -105.75) * mm, "end": v(2.75, -105.75) * mm});
            skLineSegment(sketch, "E13.3.1.0", {"start": v(2.75, -102.25) * mm, "end": v(2.75, -100.25) * mm});
            skLineSegment(sketch, "E13.3.1.1", {"start": v(0.75, -102.25) * mm, "end": v(0.75, -100.25) * mm});
            skLineSegment(sketch, "E13.3.1.2", {"start": v(0.75, -100.25) * mm, "end": v(2.75, -100.25) * mm});
            skLineSegment(sketch, "E13.3.1.3", {"start": v(0.75, -102.25) * mm, "end": v(2.75, -102.25) * mm});
            skLineSegment(sketch, "E13.3.2.0", {"start": v(2.75, -98.75) * mm, "end": v(2.75, -96.75) * mm});
            skLineSegment(sketch, "E13.3.2.1", {"start": v(0.75, -98.75) * mm, "end": v(0.75, -96.75) * mm});
            skLineSegment(sketch, "E13.3.2.2", {"start": v(0.75, -96.75) * mm, "end": v(2.75, -96.75) * mm});
            skLineSegment(sketch, "E13.3.2.3", {"start": v(0.75, -98.75) * mm, "end": v(2.75, -98.75) * mm});
            skLineSegment(sketch, "E13.3.3.0", {"start": v(2.75, -95.25) * mm, "end": v(2.75, -93.25) * mm});
            skLineSegment(sketch, "E13.3.3.1", {"start": v(0.75, -95.25) * mm, "end": v(0.75, -93.25) * mm});
            skLineSegment(sketch, "E13.3.3.2", {"start": v(0.75, -93.25) * mm, "end": v(2.75, -93.25) * mm});
            skLineSegment(sketch, "E13.3.3.3", {"start": v(0.75, -95.25) * mm, "end": v(2.75, -95.25) * mm});
            skLineSegment(sketch, "E13.3.4.0", {"start": v(2.75, -91.75) * mm, "end": v(2.75, -89.75) * mm});
            skLineSegment(sketch, "E13.3.4.1", {"start": v(0.75, -91.75) * mm, "end": v(0.75, -89.75) * mm});
            skLineSegment(sketch, "E13.3.4.2", {"start": v(0.75, -89.75) * mm, "end": v(2.75, -89.75) * mm});
            skLineSegment(sketch, "E13.3.4.3", {"start": v(0.75, -91.75) * mm, "end": v(2.75, -91.75) * mm});
            skLineSegment(sketch, "E13.3.5.0", {"start": v(2.75, -88.25) * mm, "end": v(2.75, -86.25) * mm});
            skLineSegment(sketch, "E13.3.5.1", {"start": v(0.75, -88.25) * mm, "end": v(0.75, -86.25) * mm});
            skLineSegment(sketch, "E13.3.5.2", {"start": v(0.75, -86.25) * mm, "end": v(2.75, -86.25) * mm});
            skLineSegment(sketch, "E13.3.5.3", {"start": v(0.75, -88.25) * mm, "end": v(2.75, -88.25) * mm});
            skLineSegment(sketch, "E13.3.6.0", {"start": v(2.75, -84.75) * mm, "end": v(2.75, -82.75) * mm});
            skLineSegment(sketch, "E13.3.6.1", {"start": v(0.75, -84.75) * mm, "end": v(0.75, -82.75) * mm});
            skLineSegment(sketch, "E13.3.6.2", {"start": v(0.75, -82.75) * mm, "end": v(2.75, -82.75) * mm});
            skLineSegment(sketch, "E13.3.6.3", {"start": v(0.75, -84.75) * mm, "end": v(2.75, -84.75) * mm});
            skLineSegment(sketch, "E13.3.7.0", {"start": v(2.75, -81.25) * mm, "end": v(2.75, -79.25) * mm});
            skLineSegment(sketch, "E13.3.7.1", {"start": v(0.75, -81.25) * mm, "end": v(0.75, -79.25) * mm});
            skLineSegment(sketch, "E13.3.7.2", {"start": v(0.75, -79.25) * mm, "end": v(2.75, -79.25) * mm});
            skLineSegment(sketch, "E13.3.7.3", {"start": v(0.75, -81.25) * mm, "end": v(2.75, -81.25) * mm});
            skLineSegment(sketch, "E13.3.8.0", {"start": v(2.75, -77.75) * mm, "end": v(2.75, -75.75) * mm});
            skLineSegment(sketch, "E13.3.8.1", {"start": v(0.75, -77.75) * mm, "end": v(0.75, -75.75) * mm});
            skLineSegment(sketch, "E13.3.8.2", {"start": v(0.75, -75.75) * mm, "end": v(2.75, -75.75) * mm});
            skLineSegment(sketch, "E13.3.8.3", {"start": v(0.75, -77.75) * mm, "end": v(2.75, -77.75) * mm});
            skLineSegment(sketch, "E13.3.9.0", {"start": v(2.75, -74.25) * mm, "end": v(2.75, -72.25) * mm});
            skLineSegment(sketch, "E13.3.9.1", {"start": v(0.75, -74.25) * mm, "end": v(0.75, -72.25) * mm});
            skLineSegment(sketch, "E13.3.9.2", {"start": v(0.75, -72.25) * mm, "end": v(2.75, -72.25) * mm});
            skLineSegment(sketch, "E13.3.9.3", {"start": v(0.75, -74.25) * mm, "end": v(2.75, -74.25) * mm});
            skLineSegment(sketch, "E13.3.10.0", {"start": v(2.75, -70.75) * mm, "end": v(2.75, -68.75) * mm});
            skLineSegment(sketch, "E13.3.10.1", {"start": v(0.75, -70.75) * mm, "end": v(0.75, -68.75) * mm});
            skLineSegment(sketch, "E13.3.10.2", {"start": v(0.75, -68.75) * mm, "end": v(2.75, -68.75) * mm});
            skLineSegment(sketch, "E13.3.10.3", {"start": v(0.75, -70.75) * mm, "end": v(2.75, -70.75) * mm});
            skLineSegment(sketch, "E13.3.11.0", {"start": v(2.75, -67.25) * mm, "end": v(2.75, -65.25) * mm});
            skLineSegment(sketch, "E13.3.11.1", {"start": v(0.75, -67.25) * mm, "end": v(0.75, -65.25) * mm});
            skLineSegment(sketch, "E13.3.11.2", {"start": v(0.75, -65.25) * mm, "end": v(2.75, -65.25) * mm});
            skLineSegment(sketch, "E13.3.11.3", {"start": v(0.75, -67.25) * mm, "end": v(2.75, -67.25) * mm});
            skLineSegment(sketch, "E13.3.12.0", {"start": v(2.75, -63.75) * mm, "end": v(2.75, -61.75) * mm});
            skLineSegment(sketch, "E13.3.12.1", {"start": v(0.75, -63.75) * mm, "end": v(0.75, -61.75) * mm});
            skLineSegment(sketch, "E13.3.12.2", {"start": v(0.75, -61.75) * mm, "end": v(2.75, -61.75) * mm});
            skLineSegment(sketch, "E13.3.12.3", {"start": v(0.75, -63.75) * mm, "end": v(2.75, -63.75) * mm});
            skLineSegment(sketch, "E13.3.13.0", {"start": v(2.75, -60.25) * mm, "end": v(2.75, -58.25) * mm});
            skLineSegment(sketch, "E13.3.13.1", {"start": v(0.75, -60.25) * mm, "end": v(0.75, -58.25) * mm});
            skLineSegment(sketch, "E13.3.13.2", {"start": v(0.75, -58.25) * mm, "end": v(2.75, -58.25) * mm});
            skLineSegment(sketch, "E13.3.13.3", {"start": v(0.75, -60.25) * mm, "end": v(2.75, -60.25) * mm});
            skLineSegment(sketch, "E13.3.14.0", {"start": v(2.75, -56.75) * mm, "end": v(2.75, -54.75) * mm});
            skLineSegment(sketch, "E13.3.14.1", {"start": v(0.75, -56.75) * mm, "end": v(0.75, -54.75) * mm});
            skLineSegment(sketch, "E13.3.14.2", {"start": v(0.75, -54.75) * mm, "end": v(2.75, -54.75) * mm});
            skLineSegment(sketch, "E13.3.14.3", {"start": v(0.75, -56.75) * mm, "end": v(2.75, -56.75) * mm});
            skLineSegment(sketch, "E13.3.15.0", {"start": v(2.75, -53.25) * mm, "end": v(2.75, -51.25) * mm});
            skLineSegment(sketch, "E13.3.15.1", {"start": v(0.75, -53.25) * mm, "end": v(0.75, -51.25) * mm});
            skLineSegment(sketch, "E13.3.15.2", {"start": v(0.75, -51.25) * mm, "end": v(2.75, -51.25) * mm});
            skLineSegment(sketch, "E13.3.15.3", {"start": v(0.75, -53.25) * mm, "end": v(2.75, -53.25) * mm});
            skLineSegment(sketch, "E13.3.16.0", {"start": v(2.75, -49.75) * mm, "end": v(2.75, -47.75) * mm});
            skLineSegment(sketch, "E13.3.16.1", {"start": v(0.75, -49.75) * mm, "end": v(0.75, -47.75) * mm});
            skLineSegment(sketch, "E13.3.16.2", {"start": v(0.75, -47.75) * mm, "end": v(2.75, -47.75) * mm});
            skLineSegment(sketch, "E13.3.16.3", {"start": v(0.75, -49.75) * mm, "end": v(2.75, -49.75) * mm});
            skLineSegment(sketch, "E13.3.17.0", {"start": v(2.75, -46.25) * mm, "end": v(2.75, -44.25) * mm});
            skLineSegment(sketch, "E13.3.17.1", {"start": v(0.75, -46.25) * mm, "end": v(0.75, -44.25) * mm});
            skLineSegment(sketch, "E13.3.17.2", {"start": v(0.75, -44.25) * mm, "end": v(2.75, -44.25) * mm});
            skLineSegment(sketch, "E13.3.17.3", {"start": v(0.75, -46.25) * mm, "end": v(2.75, -46.25) * mm});
            skLineSegment(sketch, "E13.3.18.0", {"start": v(2.75, -42.75) * mm, "end": v(2.75, -40.75) * mm});
            skLineSegment(sketch, "E13.3.18.1", {"start": v(0.75, -42.75) * mm, "end": v(0.75, -40.75) * mm});
            skLineSegment(sketch, "E13.3.18.2", {"start": v(0.75, -40.75) * mm, "end": v(2.75, -40.75) * mm});
            skLineSegment(sketch, "E13.3.18.3", {"start": v(0.75, -42.75) * mm, "end": v(2.75, -42.75) * mm});
            skLineSegment(sketch, "E13.3.19.0", {"start": v(2.75, -39.25) * mm, "end": v(2.75, -37.25) * mm});
            skLineSegment(sketch, "E13.3.19.1", {"start": v(0.75, -39.25) * mm, "end": v(0.75, -37.25) * mm});
            skLineSegment(sketch, "E13.3.19.2", {"start": v(0.75, -37.25) * mm, "end": v(2.75, -37.25) * mm});
            skLineSegment(sketch, "E13.3.19.3", {"start": v(0.75, -39.25) * mm, "end": v(2.75, -39.25) * mm});
            skLineSegment(sketch, "E13.3.20.0", {"start": v(2.75, -35.75) * mm, "end": v(2.75, -33.75) * mm});
            skLineSegment(sketch, "E13.3.20.1", {"start": v(0.75, -35.75) * mm, "end": v(0.75, -33.75) * mm});
            skLineSegment(sketch, "E13.3.20.2", {"start": v(0.75, -33.75) * mm, "end": v(2.75, -33.75) * mm});
            skLineSegment(sketch, "E13.3.20.3", {"start": v(0.75, -35.75) * mm, "end": v(2.75, -35.75) * mm});
            skLineSegment(sketch, "E13.3.21.0", {"start": v(2.75, -32.25) * mm, "end": v(2.75, -30.25) * mm});
            skLineSegment(sketch, "E13.3.21.1", {"start": v(0.75, -32.25) * mm, "end": v(0.75, -30.25) * mm});
            skLineSegment(sketch, "E13.3.21.2", {"start": v(0.75, -30.25) * mm, "end": v(2.75, -30.25) * mm});
            skLineSegment(sketch, "E13.3.21.3", {"start": v(0.75, -32.25) * mm, "end": v(2.75, -32.25) * mm});
            skLineSegment(sketch, "E13.3.22.0", {"start": v(2.75, -28.75) * mm, "end": v(2.75, -26.75) * mm});
            skLineSegment(sketch, "E13.3.22.1", {"start": v(0.75, -28.75) * mm, "end": v(0.75, -26.75) * mm});
            skLineSegment(sketch, "E13.3.22.2", {"start": v(0.75, -26.75) * mm, "end": v(2.75, -26.75) * mm});
            skLineSegment(sketch, "E13.3.22.3", {"start": v(0.75, -28.75) * mm, "end": v(2.75, -28.75) * mm});
            skLineSegment(sketch, "E13.3.23.0", {"start": v(2.75, -25.25) * mm, "end": v(2.75, -23.25) * mm});
            skLineSegment(sketch, "E13.3.23.1", {"start": v(0.75, -25.25) * mm, "end": v(0.75, -23.25) * mm});
            skLineSegment(sketch, "E13.3.23.2", {"start": v(0.75, -23.25) * mm, "end": v(2.75, -23.25) * mm});
            skLineSegment(sketch, "E13.3.23.3", {"start": v(0.75, -25.25) * mm, "end": v(2.75, -25.25) * mm});
            skLineSegment(sketch, "E13.3.24.0", {"start": v(2.75, -21.75) * mm, "end": v(2.75, -19.75) * mm});
            skLineSegment(sketch, "E13.3.24.1", {"start": v(0.75, -21.75) * mm, "end": v(0.75, -19.75) * mm});
            skLineSegment(sketch, "E13.3.24.2", {"start": v(0.75, -19.75) * mm, "end": v(2.75, -19.75) * mm});
            skLineSegment(sketch, "E13.3.24.3", {"start": v(0.75, -21.75) * mm, "end": v(2.75, -21.75) * mm});
            skLineSegment(sketch, "E13.4.0.0", {"start": v(6.25, -105.75) * mm, "end": v(6.25, -103.75) * mm});
            skLineSegment(sketch, "E13.4.0.1", {"start": v(4.25, -105.75) * mm, "end": v(4.25, -103.75) * mm});
            skLineSegment(sketch, "E13.4.0.2", {"start": v(4.25, -103.75) * mm, "end": v(6.25, -103.75) * mm});
            skLineSegment(sketch, "E13.4.0.3", {"start": v(4.25, -105.75) * mm, "end": v(6.25, -105.75) * mm});
            skLineSegment(sketch, "E13.4.1.0", {"start": v(6.25, -102.25) * mm, "end": v(6.25, -100.25) * mm});
            skLineSegment(sketch, "E13.4.1.1", {"start": v(4.25, -102.25) * mm, "end": v(4.25, -100.25) * mm});
            skLineSegment(sketch, "E13.4.1.2", {"start": v(4.25, -100.25) * mm, "end": v(6.25, -100.25) * mm});
            skLineSegment(sketch, "E13.4.1.3", {"start": v(4.25, -102.25) * mm, "end": v(6.25, -102.25) * mm});
            skLineSegment(sketch, "E13.4.2.0", {"start": v(6.25, -98.75) * mm, "end": v(6.25, -96.75) * mm});
            skLineSegment(sketch, "E13.4.2.1", {"start": v(4.25, -98.75) * mm, "end": v(4.25, -96.75) * mm});
            skLineSegment(sketch, "E13.4.2.2", {"start": v(4.25, -96.75) * mm, "end": v(6.25, -96.75) * mm});
            skLineSegment(sketch, "E13.4.2.3", {"start": v(4.25, -98.75) * mm, "end": v(6.25, -98.75) * mm});
            skLineSegment(sketch, "E13.4.3.0", {"start": v(6.25, -95.25) * mm, "end": v(6.25, -93.25) * mm});
            skLineSegment(sketch, "E13.4.3.1", {"start": v(4.25, -95.25) * mm, "end": v(4.25, -93.25) * mm});
            skLineSegment(sketch, "E13.4.3.2", {"start": v(4.25, -93.25) * mm, "end": v(6.25, -93.25) * mm});
            skLineSegment(sketch, "E13.4.3.3", {"start": v(4.25, -95.25) * mm, "end": v(6.25, -95.25) * mm});
            skLineSegment(sketch, "E13.4.4.0", {"start": v(6.25, -91.75) * mm, "end": v(6.25, -89.75) * mm});
            skLineSegment(sketch, "E13.4.4.1", {"start": v(4.25, -91.75) * mm, "end": v(4.25, -89.75) * mm});
            skLineSegment(sketch, "E13.4.4.2", {"start": v(4.25, -89.75) * mm, "end": v(6.25, -89.75) * mm});
            skLineSegment(sketch, "E13.4.4.3", {"start": v(4.25, -91.75) * mm, "end": v(6.25, -91.75) * mm});
            skLineSegment(sketch, "E13.4.5.0", {"start": v(6.25, -88.25) * mm, "end": v(6.25, -86.25) * mm});
            skLineSegment(sketch, "E13.4.5.1", {"start": v(4.25, -88.25) * mm, "end": v(4.25, -86.25) * mm});
            skLineSegment(sketch, "E13.4.5.2", {"start": v(4.25, -86.25) * mm, "end": v(6.25, -86.25) * mm});
            skLineSegment(sketch, "E13.4.5.3", {"start": v(4.25, -88.25) * mm, "end": v(6.25, -88.25) * mm});
            skLineSegment(sketch, "E13.4.6.0", {"start": v(6.25, -84.75) * mm, "end": v(6.25, -82.75) * mm});
            skLineSegment(sketch, "E13.4.6.1", {"start": v(4.25, -84.75) * mm, "end": v(4.25, -82.75) * mm});
            skLineSegment(sketch, "E13.4.6.2", {"start": v(4.25, -82.75) * mm, "end": v(6.25, -82.75) * mm});
            skLineSegment(sketch, "E13.4.6.3", {"start": v(4.25, -84.75) * mm, "end": v(6.25, -84.75) * mm});
            skLineSegment(sketch, "E13.4.7.0", {"start": v(6.25, -81.25) * mm, "end": v(6.25, -79.25) * mm});
            skLineSegment(sketch, "E13.4.7.1", {"start": v(4.25, -81.25) * mm, "end": v(4.25, -79.25) * mm});
            skLineSegment(sketch, "E13.4.7.2", {"start": v(4.25, -79.25) * mm, "end": v(6.25, -79.25) * mm});
            skLineSegment(sketch, "E13.4.7.3", {"start": v(4.25, -81.25) * mm, "end": v(6.25, -81.25) * mm});
            skLineSegment(sketch, "E13.4.8.0", {"start": v(6.25, -77.75) * mm, "end": v(6.25, -75.75) * mm});
            skLineSegment(sketch, "E13.4.8.1", {"start": v(4.25, -77.75) * mm, "end": v(4.25, -75.75) * mm});
            skLineSegment(sketch, "E13.4.8.2", {"start": v(4.25, -75.75) * mm, "end": v(6.25, -75.75) * mm});
            skLineSegment(sketch, "E13.4.8.3", {"start": v(4.25, -77.75) * mm, "end": v(6.25, -77.75) * mm});
            skLineSegment(sketch, "E13.4.9.0", {"start": v(6.25, -74.25) * mm, "end": v(6.25, -72.25) * mm});
            skLineSegment(sketch, "E13.4.9.1", {"start": v(4.25, -74.25) * mm, "end": v(4.25, -72.25) * mm});
            skLineSegment(sketch, "E13.4.9.2", {"start": v(4.25, -72.25) * mm, "end": v(6.25, -72.25) * mm});
            skLineSegment(sketch, "E13.4.9.3", {"start": v(4.25, -74.25) * mm, "end": v(6.25, -74.25) * mm});
            skLineSegment(sketch, "E13.4.10.0", {"start": v(6.25, -70.75) * mm, "end": v(6.25, -68.75) * mm});
            skLineSegment(sketch, "E13.4.10.1", {"start": v(4.25, -70.75) * mm, "end": v(4.25, -68.75) * mm});
            skLineSegment(sketch, "E13.4.10.2", {"start": v(4.25, -68.75) * mm, "end": v(6.25, -68.75) * mm});
            skLineSegment(sketch, "E13.4.10.3", {"start": v(4.25, -70.75) * mm, "end": v(6.25, -70.75) * mm});
            skLineSegment(sketch, "E13.4.11.0", {"start": v(6.25, -67.25) * mm, "end": v(6.25, -65.25) * mm});
            skLineSegment(sketch, "E13.4.11.1", {"start": v(4.25, -67.25) * mm, "end": v(4.25, -65.25) * mm});
            skLineSegment(sketch, "E13.4.11.2", {"start": v(4.25, -65.25) * mm, "end": v(6.25, -65.25) * mm});
            skLineSegment(sketch, "E13.4.11.3", {"start": v(4.25, -67.25) * mm, "end": v(6.25, -67.25) * mm});
            skLineSegment(sketch, "E13.4.12.0", {"start": v(6.25, -63.75) * mm, "end": v(6.25, -61.75) * mm});
            skLineSegment(sketch, "E13.4.12.1", {"start": v(4.25, -63.75) * mm, "end": v(4.25, -61.75) * mm});
            skLineSegment(sketch, "E13.4.12.2", {"start": v(4.25, -61.75) * mm, "end": v(6.25, -61.75) * mm});
            skLineSegment(sketch, "E13.4.12.3", {"start": v(4.25, -63.75) * mm, "end": v(6.25, -63.75) * mm});
            skLineSegment(sketch, "E13.4.13.0", {"start": v(6.25, -60.25) * mm, "end": v(6.25, -58.25) * mm});
            skLineSegment(sketch, "E13.4.13.1", {"start": v(4.25, -60.25) * mm, "end": v(4.25, -58.25) * mm});
            skLineSegment(sketch, "E13.4.13.2", {"start": v(4.25, -58.25) * mm, "end": v(6.25, -58.25) * mm});
            skLineSegment(sketch, "E13.4.13.3", {"start": v(4.25, -60.25) * mm, "end": v(6.25, -60.25) * mm});
            skLineSegment(sketch, "E13.4.14.0", {"start": v(6.25, -56.75) * mm, "end": v(6.25, -54.75) * mm});
            skLineSegment(sketch, "E13.4.14.1", {"start": v(4.25, -56.75) * mm, "end": v(4.25, -54.75) * mm});
            skLineSegment(sketch, "E13.4.14.2", {"start": v(4.25, -54.75) * mm, "end": v(6.25, -54.75) * mm});
            skLineSegment(sketch, "E13.4.14.3", {"start": v(4.25, -56.75) * mm, "end": v(6.25, -56.75) * mm});
            skLineSegment(sketch, "E13.4.15.0", {"start": v(6.25, -53.25) * mm, "end": v(6.25, -51.25) * mm});
            skLineSegment(sketch, "E13.4.15.1", {"start": v(4.25, -53.25) * mm, "end": v(4.25, -51.25) * mm});
            skLineSegment(sketch, "E13.4.15.2", {"start": v(4.25, -51.25) * mm, "end": v(6.25, -51.25) * mm});
            skLineSegment(sketch, "E13.4.15.3", {"start": v(4.25, -53.25) * mm, "end": v(6.25, -53.25) * mm});
            skLineSegment(sketch, "E13.4.16.0", {"start": v(6.25, -49.75) * mm, "end": v(6.25, -47.75) * mm});
            skLineSegment(sketch, "E13.4.16.1", {"start": v(4.25, -49.75) * mm, "end": v(4.25, -47.75) * mm});
            skLineSegment(sketch, "E13.4.16.2", {"start": v(4.25, -47.75) * mm, "end": v(6.25, -47.75) * mm});
            skLineSegment(sketch, "E13.4.16.3", {"start": v(4.25, -49.75) * mm, "end": v(6.25, -49.75) * mm});
            skLineSegment(sketch, "E13.4.17.0", {"start": v(6.25, -46.25) * mm, "end": v(6.25, -44.25) * mm});
            skLineSegment(sketch, "E13.4.17.1", {"start": v(4.25, -46.25) * mm, "end": v(4.25, -44.25) * mm});
            skLineSegment(sketch, "E13.4.17.2", {"start": v(4.25, -44.25) * mm, "end": v(6.25, -44.25) * mm});
            skLineSegment(sketch, "E13.4.17.3", {"start": v(4.25, -46.25) * mm, "end": v(6.25, -46.25) * mm});
            skLineSegment(sketch, "E13.4.18.0", {"start": v(6.25, -42.75) * mm, "end": v(6.25, -40.75) * mm});
            skLineSegment(sketch, "E13.4.18.1", {"start": v(4.25, -42.75) * mm, "end": v(4.25, -40.75) * mm});
            skLineSegment(sketch, "E13.4.18.2", {"start": v(4.25, -40.75) * mm, "end": v(6.25, -40.75) * mm});
            skLineSegment(sketch, "E13.4.18.3", {"start": v(4.25, -42.75) * mm, "end": v(6.25, -42.75) * mm});
            skLineSegment(sketch, "E13.4.19.0", {"start": v(6.25, -39.25) * mm, "end": v(6.25, -37.25) * mm});
            skLineSegment(sketch, "E13.4.19.1", {"start": v(4.25, -39.25) * mm, "end": v(4.25, -37.25) * mm});
            skLineSegment(sketch, "E13.4.19.2", {"start": v(4.25, -37.25) * mm, "end": v(6.25, -37.25) * mm});
            skLineSegment(sketch, "E13.4.19.3", {"start": v(4.25, -39.25) * mm, "end": v(6.25, -39.25) * mm});
            skLineSegment(sketch, "E13.4.20.0", {"start": v(6.25, -35.75) * mm, "end": v(6.25, -33.75) * mm});
            skLineSegment(sketch, "E13.4.20.1", {"start": v(4.25, -35.75) * mm, "end": v(4.25, -33.75) * mm});
            skLineSegment(sketch, "E13.4.20.2", {"start": v(4.25, -33.75) * mm, "end": v(6.25, -33.75) * mm});
            skLineSegment(sketch, "E13.4.20.3", {"start": v(4.25, -35.75) * mm, "end": v(6.25, -35.75) * mm});
            skLineSegment(sketch, "E13.4.21.0", {"start": v(6.25, -32.25) * mm, "end": v(6.25, -30.25) * mm});
            skLineSegment(sketch, "E13.4.21.1", {"start": v(4.25, -32.25) * mm, "end": v(4.25, -30.25) * mm});
            skLineSegment(sketch, "E13.4.21.2", {"start": v(4.25, -30.25) * mm, "end": v(6.25, -30.25) * mm});
            skLineSegment(sketch, "E13.4.21.3", {"start": v(4.25, -32.25) * mm, "end": v(6.25, -32.25) * mm});
            skLineSegment(sketch, "E13.4.22.0", {"start": v(6.25, -28.75) * mm, "end": v(6.25, -26.75) * mm});
            skLineSegment(sketch, "E13.4.22.1", {"start": v(4.25, -28.75) * mm, "end": v(4.25, -26.75) * mm});
            skLineSegment(sketch, "E13.4.22.2", {"start": v(4.25, -26.75) * mm, "end": v(6.25, -26.75) * mm});
            skLineSegment(sketch, "E13.4.22.3", {"start": v(4.25, -28.75) * mm, "end": v(6.25, -28.75) * mm});
            skLineSegment(sketch, "E13.4.23.0", {"start": v(6.25, -25.25) * mm, "end": v(6.25, -23.25) * mm});
            skLineSegment(sketch, "E13.4.23.1", {"start": v(4.25, -25.25) * mm, "end": v(4.25, -23.25) * mm});
            skLineSegment(sketch, "E13.4.23.2", {"start": v(4.25, -23.25) * mm, "end": v(6.25, -23.25) * mm});
            skLineSegment(sketch, "E13.4.23.3", {"start": v(4.25, -25.25) * mm, "end": v(6.25, -25.25) * mm});
            skLineSegment(sketch, "E13.4.24.0", {"start": v(6.25, -21.75) * mm, "end": v(6.25, -19.75) * mm});
            skLineSegment(sketch, "E13.4.24.1", {"start": v(4.25, -21.75) * mm, "end": v(4.25, -19.75) * mm});
            skLineSegment(sketch, "E13.4.24.2", {"start": v(4.25, -19.75) * mm, "end": v(6.25, -19.75) * mm});
            skLineSegment(sketch, "E13.4.24.3", {"start": v(4.25, -21.75) * mm, "end": v(6.25, -21.75) * mm});
            skLineSegment(sketch, "E13.5.0.0", {"start": v(9.75, -105.75) * mm, "end": v(9.75, -103.75) * mm});
            skLineSegment(sketch, "E13.5.0.1", {"start": v(7.75, -105.75) * mm, "end": v(7.75, -103.75) * mm});
            skLineSegment(sketch, "E13.5.0.2", {"start": v(7.75, -103.75) * mm, "end": v(9.75, -103.75) * mm});
            skLineSegment(sketch, "E13.5.0.3", {"start": v(7.75, -105.75) * mm, "end": v(9.75, -105.75) * mm});
            skLineSegment(sketch, "E13.5.1.0", {"start": v(9.75, -102.25) * mm, "end": v(9.75, -100.25) * mm});
            skLineSegment(sketch, "E13.5.1.1", {"start": v(7.75, -102.25) * mm, "end": v(7.75, -100.25) * mm});
            skLineSegment(sketch, "E13.5.1.2", {"start": v(7.75, -100.25) * mm, "end": v(9.75, -100.25) * mm});
            skLineSegment(sketch, "E13.5.1.3", {"start": v(7.75, -102.25) * mm, "end": v(9.75, -102.25) * mm});
            skLineSegment(sketch, "E13.5.2.0", {"start": v(9.75, -98.75) * mm, "end": v(9.75, -96.75) * mm});
            skLineSegment(sketch, "E13.5.2.1", {"start": v(7.75, -98.75) * mm, "end": v(7.75, -96.75) * mm});
            skLineSegment(sketch, "E13.5.2.2", {"start": v(7.75, -96.75) * mm, "end": v(9.75, -96.75) * mm});
            skLineSegment(sketch, "E13.5.2.3", {"start": v(7.75, -98.75) * mm, "end": v(9.75, -98.75) * mm});
            skLineSegment(sketch, "E13.5.3.0", {"start": v(9.75, -95.25) * mm, "end": v(9.75, -93.25) * mm});
            skLineSegment(sketch, "E13.5.3.1", {"start": v(7.75, -95.25) * mm, "end": v(7.75, -93.25) * mm});
            skLineSegment(sketch, "E13.5.3.2", {"start": v(7.75, -93.25) * mm, "end": v(9.75, -93.25) * mm});
            skLineSegment(sketch, "E13.5.3.3", {"start": v(7.75, -95.25) * mm, "end": v(9.75, -95.25) * mm});
            skLineSegment(sketch, "E13.5.4.0", {"start": v(9.75, -91.75) * mm, "end": v(9.75, -89.75) * mm});
            skLineSegment(sketch, "E13.5.4.1", {"start": v(7.75, -91.75) * mm, "end": v(7.75, -89.75) * mm});
            skLineSegment(sketch, "E13.5.4.2", {"start": v(7.75, -89.75) * mm, "end": v(9.75, -89.75) * mm});
            skLineSegment(sketch, "E13.5.4.3", {"start": v(7.75, -91.75) * mm, "end": v(9.75, -91.75) * mm});
            skLineSegment(sketch, "E13.5.5.0", {"start": v(9.75, -88.25) * mm, "end": v(9.75, -86.25) * mm});
            skLineSegment(sketch, "E13.5.5.1", {"start": v(7.75, -88.25) * mm, "end": v(7.75, -86.25) * mm});
            skLineSegment(sketch, "E13.5.5.2", {"start": v(7.75, -86.25) * mm, "end": v(9.75, -86.25) * mm});
            skLineSegment(sketch, "E13.5.5.3", {"start": v(7.75, -88.25) * mm, "end": v(9.75, -88.25) * mm});
            skLineSegment(sketch, "E13.5.6.0", {"start": v(9.75, -84.75) * mm, "end": v(9.75, -82.75) * mm});
            skLineSegment(sketch, "E13.5.6.1", {"start": v(7.75, -84.75) * mm, "end": v(7.75, -82.75) * mm});
            skLineSegment(sketch, "E13.5.6.2", {"start": v(7.75, -82.75) * mm, "end": v(9.75, -82.75) * mm});
            skLineSegment(sketch, "E13.5.6.3", {"start": v(7.75, -84.75) * mm, "end": v(9.75, -84.75) * mm});
            skLineSegment(sketch, "E13.5.7.0", {"start": v(9.75, -81.25) * mm, "end": v(9.75, -79.25) * mm});
            skLineSegment(sketch, "E13.5.7.1", {"start": v(7.75, -81.25) * mm, "end": v(7.75, -79.25) * mm});
            skLineSegment(sketch, "E13.5.7.2", {"start": v(7.75, -79.25) * mm, "end": v(9.75, -79.25) * mm});
            skLineSegment(sketch, "E13.5.7.3", {"start": v(7.75, -81.25) * mm, "end": v(9.75, -81.25) * mm});
            skLineSegment(sketch, "E13.5.8.0", {"start": v(9.75, -77.75) * mm, "end": v(9.75, -75.75) * mm});
            skLineSegment(sketch, "E13.5.8.1", {"start": v(7.75, -77.75) * mm, "end": v(7.75, -75.75) * mm});
            skLineSegment(sketch, "E13.5.8.2", {"start": v(7.75, -75.75) * mm, "end": v(9.75, -75.75) * mm});
            skLineSegment(sketch, "E13.5.8.3", {"start": v(7.75, -77.75) * mm, "end": v(9.75, -77.75) * mm});
            skLineSegment(sketch, "E13.5.9.0", {"start": v(9.75, -74.25) * mm, "end": v(9.75, -72.25) * mm});
            skLineSegment(sketch, "E13.5.9.1", {"start": v(7.75, -74.25) * mm, "end": v(7.75, -72.25) * mm});
            skLineSegment(sketch, "E13.5.9.2", {"start": v(7.75, -72.25) * mm, "end": v(9.75, -72.25) * mm});
            skLineSegment(sketch, "E13.5.9.3", {"start": v(7.75, -74.25) * mm, "end": v(9.75, -74.25) * mm});
            skLineSegment(sketch, "E13.5.10.0", {"start": v(9.75, -70.75) * mm, "end": v(9.75, -68.75) * mm});
            skLineSegment(sketch, "E13.5.10.1", {"start": v(7.75, -70.75) * mm, "end": v(7.75, -68.75) * mm});
            skLineSegment(sketch, "E13.5.10.2", {"start": v(7.75, -68.75) * mm, "end": v(9.75, -68.75) * mm});
            skLineSegment(sketch, "E13.5.10.3", {"start": v(7.75, -70.75) * mm, "end": v(9.75, -70.75) * mm});
            skLineSegment(sketch, "E13.5.11.0", {"start": v(9.75, -67.25) * mm, "end": v(9.75, -65.25) * mm});
            skLineSegment(sketch, "E13.5.11.1", {"start": v(7.75, -67.25) * mm, "end": v(7.75, -65.25) * mm});
            skLineSegment(sketch, "E13.5.11.2", {"start": v(7.75, -65.25) * mm, "end": v(9.75, -65.25) * mm});
            skLineSegment(sketch, "E13.5.11.3", {"start": v(7.75, -67.25) * mm, "end": v(9.75, -67.25) * mm});
            skLineSegment(sketch, "E13.5.12.0", {"start": v(9.75, -63.75) * mm, "end": v(9.75, -61.75) * mm});
            skLineSegment(sketch, "E13.5.12.1", {"start": v(7.75, -63.75) * mm, "end": v(7.75, -61.75) * mm});
            skLineSegment(sketch, "E13.5.12.2", {"start": v(7.75, -61.75) * mm, "end": v(9.75, -61.75) * mm});
            skLineSegment(sketch, "E13.5.12.3", {"start": v(7.75, -63.75) * mm, "end": v(9.75, -63.75) * mm});
            skLineSegment(sketch, "E13.5.13.0", {"start": v(9.75, -60.25) * mm, "end": v(9.75, -58.25) * mm});
            skLineSegment(sketch, "E13.5.13.1", {"start": v(7.75, -60.25) * mm, "end": v(7.75, -58.25) * mm});
            skLineSegment(sketch, "E13.5.13.2", {"start": v(7.75, -58.25) * mm, "end": v(9.75, -58.25) * mm});
            skLineSegment(sketch, "E13.5.13.3", {"start": v(7.75, -60.25) * mm, "end": v(9.75, -60.25) * mm});
            skLineSegment(sketch, "E13.5.14.0", {"start": v(9.75, -56.75) * mm, "end": v(9.75, -54.75) * mm});
            skLineSegment(sketch, "E13.5.14.1", {"start": v(7.75, -56.75) * mm, "end": v(7.75, -54.75) * mm});
            skLineSegment(sketch, "E13.5.14.2", {"start": v(7.75, -54.75) * mm, "end": v(9.75, -54.75) * mm});
            skLineSegment(sketch, "E13.5.14.3", {"start": v(7.75, -56.75) * mm, "end": v(9.75, -56.75) * mm});
            skLineSegment(sketch, "E13.5.15.0", {"start": v(9.75, -53.25) * mm, "end": v(9.75, -51.25) * mm});
            skLineSegment(sketch, "E13.5.15.1", {"start": v(7.75, -53.25) * mm, "end": v(7.75, -51.25) * mm});
            skLineSegment(sketch, "E13.5.15.2", {"start": v(7.75, -51.25) * mm, "end": v(9.75, -51.25) * mm});
            skLineSegment(sketch, "E13.5.15.3", {"start": v(7.75, -53.25) * mm, "end": v(9.75, -53.25) * mm});
            skLineSegment(sketch, "E13.5.16.0", {"start": v(9.75, -49.75) * mm, "end": v(9.75, -47.75) * mm});
            skLineSegment(sketch, "E13.5.16.1", {"start": v(7.75, -49.75) * mm, "end": v(7.75, -47.75) * mm});
            skLineSegment(sketch, "E13.5.16.2", {"start": v(7.75, -47.75) * mm, "end": v(9.75, -47.75) * mm});
            skLineSegment(sketch, "E13.5.16.3", {"start": v(7.75, -49.75) * mm, "end": v(9.75, -49.75) * mm});
            skLineSegment(sketch, "E13.5.17.0", {"start": v(9.75, -46.25) * mm, "end": v(9.75, -44.25) * mm});
            skLineSegment(sketch, "E13.5.17.1", {"start": v(7.75, -46.25) * mm, "end": v(7.75, -44.25) * mm});
            skLineSegment(sketch, "E13.5.17.2", {"start": v(7.75, -44.25) * mm, "end": v(9.75, -44.25) * mm});
            skLineSegment(sketch, "E13.5.17.3", {"start": v(7.75, -46.25) * mm, "end": v(9.75, -46.25) * mm});
            skLineSegment(sketch, "E13.5.18.0", {"start": v(9.75, -42.75) * mm, "end": v(9.75, -40.75) * mm});
            skLineSegment(sketch, "E13.5.18.1", {"start": v(7.75, -42.75) * mm, "end": v(7.75, -40.75) * mm});
            skLineSegment(sketch, "E13.5.18.2", {"start": v(7.75, -40.75) * mm, "end": v(9.75, -40.75) * mm});
            skLineSegment(sketch, "E13.5.18.3", {"start": v(7.75, -42.75) * mm, "end": v(9.75, -42.75) * mm});
            skLineSegment(sketch, "E13.5.19.0", {"start": v(9.75, -39.25) * mm, "end": v(9.75, -37.25) * mm});
            skLineSegment(sketch, "E13.5.19.1", {"start": v(7.75, -39.25) * mm, "end": v(7.75, -37.25) * mm});
            skLineSegment(sketch, "E13.5.19.2", {"start": v(7.75, -37.25) * mm, "end": v(9.75, -37.25) * mm});
            skLineSegment(sketch, "E13.5.19.3", {"start": v(7.75, -39.25) * mm, "end": v(9.75, -39.25) * mm});
            skLineSegment(sketch, "E13.5.20.0", {"start": v(9.75, -35.75) * mm, "end": v(9.75, -33.75) * mm});
            skLineSegment(sketch, "E13.5.20.1", {"start": v(7.75, -35.75) * mm, "end": v(7.75, -33.75) * mm});
            skLineSegment(sketch, "E13.5.20.2", {"start": v(7.75, -33.75) * mm, "end": v(9.75, -33.75) * mm});
            skLineSegment(sketch, "E13.5.20.3", {"start": v(7.75, -35.75) * mm, "end": v(9.75, -35.75) * mm});
            skLineSegment(sketch, "E13.5.21.0", {"start": v(9.75, -32.25) * mm, "end": v(9.75, -30.25) * mm});
            skLineSegment(sketch, "E13.5.21.1", {"start": v(7.75, -32.25) * mm, "end": v(7.75, -30.25) * mm});
            skLineSegment(sketch, "E13.5.21.2", {"start": v(7.75, -30.25) * mm, "end": v(9.75, -30.25) * mm});
            skLineSegment(sketch, "E13.5.21.3", {"start": v(7.75, -32.25) * mm, "end": v(9.75, -32.25) * mm});
            skLineSegment(sketch, "E13.5.22.0", {"start": v(9.75, -28.75) * mm, "end": v(9.75, -26.75) * mm});
            skLineSegment(sketch, "E13.5.22.1", {"start": v(7.75, -28.75) * mm, "end": v(7.75, -26.75) * mm});
            skLineSegment(sketch, "E13.5.22.2", {"start": v(7.75, -26.75) * mm, "end": v(9.75, -26.75) * mm});
            skLineSegment(sketch, "E13.5.22.3", {"start": v(7.75, -28.75) * mm, "end": v(9.75, -28.75) * mm});
            skLineSegment(sketch, "E13.5.23.0", {"start": v(9.75, -25.25) * mm, "end": v(9.75, -23.25) * mm});
            skLineSegment(sketch, "E13.5.23.1", {"start": v(7.75, -25.25) * mm, "end": v(7.75, -23.25) * mm});
            skLineSegment(sketch, "E13.5.23.2", {"start": v(7.75, -23.25) * mm, "end": v(9.75, -23.25) * mm});
            skLineSegment(sketch, "E13.5.23.3", {"start": v(7.75, -25.25) * mm, "end": v(9.75, -25.25) * mm});
            skLineSegment(sketch, "E13.5.24.0", {"start": v(9.75, -21.75) * mm, "end": v(9.75, -19.75) * mm});
            skLineSegment(sketch, "E13.5.24.1", {"start": v(7.75, -21.75) * mm, "end": v(7.75, -19.75) * mm});
            skLineSegment(sketch, "E13.5.24.2", {"start": v(7.75, -19.75) * mm, "end": v(9.75, -19.75) * mm});
            skLineSegment(sketch, "E13.5.24.3", {"start": v(7.75, -21.75) * mm, "end": v(9.75, -21.75) * mm});
            skLineSegment(sketch, "E13.direction1", {"start": v(-9.75, -105.75) * mm, "end": v(-6.25, -105.75) * mm, "construction": true});
            skLineSegment(sketch, "E13.direction2", {"start": v(-9.75, -105.75) * mm, "end": v(-9.75, -102.25) * mm, "construction": true});
            skLineSegment(sketch, "E14.0.0.25", {"start": v(-7.75, -18.25) * mm, "end": v(-7.75, -16.25) * mm});
            skLineSegment(sketch, "E14.3.0.25", {"start": v(-9.75, -18.25) * mm, "end": v(-9.75, -16.25) * mm});
            skLineSegment(sketch, "E14.6.0.25", {"start": v(-9.75, -16.25) * mm, "end": v(-7.75, -16.25) * mm});
            skLineSegment(sketch, "E14.9.0.25", {"start": v(-9.75, -18.25) * mm, "end": v(-7.75, -18.25) * mm});
            skLineSegment(sketch, "E14.0.0.26", {"start": v(-7.75, -14.75) * mm, "end": v(-7.75, -12.75) * mm});
            skLineSegment(sketch, "E14.3.0.26", {"start": v(-9.75, -14.75) * mm, "end": v(-9.75, -12.75) * mm});
            skLineSegment(sketch, "E14.6.0.26", {"start": v(-9.75, -12.75) * mm, "end": v(-7.75, -12.75) * mm});
            skLineSegment(sketch, "E14.9.0.26", {"start": v(-9.75, -14.75) * mm, "end": v(-7.75, -14.75) * mm});
            skLineSegment(sketch, "E14.0.0.27", {"start": v(-7.75, -11.25) * mm, "end": v(-7.75, -9.25) * mm});
            skLineSegment(sketch, "E14.3.0.27", {"start": v(-9.75, -11.25) * mm, "end": v(-9.75, -9.25) * mm});
            skLineSegment(sketch, "E14.6.0.27", {"start": v(-9.75, -9.25) * mm, "end": v(-7.75, -9.25) * mm});
            skLineSegment(sketch, "E14.9.0.27", {"start": v(-9.75, -11.25) * mm, "end": v(-7.75, -11.25) * mm});
            skLineSegment(sketch, "E14.0.0.28", {"start": v(-7.75, -7.75) * mm, "end": v(-7.75, -5.75) * mm});
            skLineSegment(sketch, "E14.3.0.28", {"start": v(-9.75, -7.75) * mm, "end": v(-9.75, -5.75) * mm});
            skLineSegment(sketch, "E14.6.0.28", {"start": v(-9.75, -5.75) * mm, "end": v(-7.75, -5.75) * mm});
            skLineSegment(sketch, "E14.9.0.28", {"start": v(-9.75, -7.75) * mm, "end": v(-7.75, -7.75) * mm});
            skLineSegment(sketch, "E14.0.0.29", {"start": v(-7.75, -4.25) * mm, "end": v(-7.75, -2.25) * mm});
            skLineSegment(sketch, "E14.3.0.29", {"start": v(-9.75, -4.25) * mm, "end": v(-9.75, -2.25) * mm});
            skLineSegment(sketch, "E14.6.0.29", {"start": v(-9.75, -2.25) * mm, "end": v(-7.75, -2.25) * mm});
            skLineSegment(sketch, "E14.9.0.29", {"start": v(-9.75, -4.25) * mm, "end": v(-7.75, -4.25) * mm});
            skLineSegment(sketch, "E14.0.1.25", {"start": v(-4.25, -18.25) * mm, "end": v(-4.25, -16.25) * mm});
            skLineSegment(sketch, "E14.3.1.25", {"start": v(-6.25, -18.25) * mm, "end": v(-6.25, -16.25) * mm});
            skLineSegment(sketch, "E14.6.1.25", {"start": v(-6.25, -16.25) * mm, "end": v(-4.25, -16.25) * mm});
            skLineSegment(sketch, "E14.9.1.25", {"start": v(-6.25, -18.25) * mm, "end": v(-4.25, -18.25) * mm});
            skLineSegment(sketch, "E14.0.1.26", {"start": v(-4.25, -14.75) * mm, "end": v(-4.25, -12.75) * mm});
            skLineSegment(sketch, "E14.3.1.26", {"start": v(-6.25, -14.75) * mm, "end": v(-6.25, -12.75) * mm});
            skLineSegment(sketch, "E14.6.1.26", {"start": v(-6.25, -12.75) * mm, "end": v(-4.25, -12.75) * mm});
            skLineSegment(sketch, "E14.9.1.26", {"start": v(-6.25, -14.75) * mm, "end": v(-4.25, -14.75) * mm});
            skLineSegment(sketch, "E14.0.1.27", {"start": v(-4.25, -11.25) * mm, "end": v(-4.25, -9.25) * mm});
            skLineSegment(sketch, "E14.3.1.27", {"start": v(-6.25, -11.25) * mm, "end": v(-6.25, -9.25) * mm});
            skLineSegment(sketch, "E14.6.1.27", {"start": v(-6.25, -9.25) * mm, "end": v(-4.25, -9.25) * mm});
            skLineSegment(sketch, "E14.9.1.27", {"start": v(-6.25, -11.25) * mm, "end": v(-4.25, -11.25) * mm});
            skLineSegment(sketch, "E14.0.1.28", {"start": v(-4.25, -7.75) * mm, "end": v(-4.25, -5.75) * mm});
            skLineSegment(sketch, "E14.3.1.28", {"start": v(-6.25, -7.75) * mm, "end": v(-6.25, -5.75) * mm});
            skLineSegment(sketch, "E14.6.1.28", {"start": v(-6.25, -5.75) * mm, "end": v(-4.25, -5.75) * mm});
            skLineSegment(sketch, "E14.9.1.28", {"start": v(-6.25, -7.75) * mm, "end": v(-4.25, -7.75) * mm});
            skLineSegment(sketch, "E14.0.1.29", {"start": v(-4.25, -4.25) * mm, "end": v(-4.25, -2.25) * mm});
            skLineSegment(sketch, "E14.3.1.29", {"start": v(-6.25, -4.25) * mm, "end": v(-6.25, -2.25) * mm});
            skLineSegment(sketch, "E14.6.1.29", {"start": v(-6.25, -2.25) * mm, "end": v(-4.25, -2.25) * mm});
            skLineSegment(sketch, "E14.9.1.29", {"start": v(-6.25, -4.25) * mm, "end": v(-4.25, -4.25) * mm});
            skLineSegment(sketch, "E14.0.2.25", {"start": v(-0.75, -18.25) * mm, "end": v(-0.75, -16.25) * mm});
            skLineSegment(sketch, "E14.3.2.25", {"start": v(-2.75, -18.25) * mm, "end": v(-2.75, -16.25) * mm});
            skLineSegment(sketch, "E14.6.2.25", {"start": v(-2.75, -16.25) * mm, "end": v(-0.75, -16.25) * mm});
            skLineSegment(sketch, "E14.9.2.25", {"start": v(-2.75, -18.25) * mm, "end": v(-0.75, -18.25) * mm});
            skLineSegment(sketch, "E14.0.2.26", {"start": v(-0.75, -14.75) * mm, "end": v(-0.75, -12.75) * mm});
            skLineSegment(sketch, "E14.3.2.26", {"start": v(-2.75, -14.75) * mm, "end": v(-2.75, -12.75) * mm});
            skLineSegment(sketch, "E14.6.2.26", {"start": v(-2.75, -12.75) * mm, "end": v(-0.75, -12.75) * mm});
            skLineSegment(sketch, "E14.9.2.26", {"start": v(-2.75, -14.75) * mm, "end": v(-0.75, -14.75) * mm});
            skLineSegment(sketch, "E14.0.2.27", {"start": v(-0.75, -11.25) * mm, "end": v(-0.75, -9.25) * mm});
            skLineSegment(sketch, "E14.3.2.27", {"start": v(-2.75, -11.25) * mm, "end": v(-2.75, -9.25) * mm});
            skLineSegment(sketch, "E14.6.2.27", {"start": v(-2.75, -9.25) * mm, "end": v(-0.75, -9.25) * mm});
            skLineSegment(sketch, "E14.9.2.27", {"start": v(-2.75, -11.25) * mm, "end": v(-0.75, -11.25) * mm});
            skLineSegment(sketch, "E14.0.2.28", {"start": v(-0.75, -7.75) * mm, "end": v(-0.75, -5.75) * mm});
            skLineSegment(sketch, "E14.3.2.28", {"start": v(-2.75, -7.75) * mm, "end": v(-2.75, -5.75) * mm});
            skLineSegment(sketch, "E14.6.2.28", {"start": v(-2.75, -5.75) * mm, "end": v(-0.75, -5.75) * mm});
            skLineSegment(sketch, "E14.9.2.28", {"start": v(-2.75, -7.75) * mm, "end": v(-0.75, -7.75) * mm});
            skLineSegment(sketch, "E14.0.2.29", {"start": v(-0.75, -4.25) * mm, "end": v(-0.75, -2.25) * mm});
            skLineSegment(sketch, "E14.3.2.29", {"start": v(-2.75, -4.25) * mm, "end": v(-2.75, -2.25) * mm});
            skLineSegment(sketch, "E14.6.2.29", {"start": v(-2.75, -2.25) * mm, "end": v(-0.75, -2.25) * mm});
            skLineSegment(sketch, "E14.9.2.29", {"start": v(-2.75, -4.25) * mm, "end": v(-0.75, -4.25) * mm});
            skLineSegment(sketch, "E14.0.3.25", {"start": v(2.75, -18.25) * mm, "end": v(2.75, -16.25) * mm});
            skLineSegment(sketch, "E14.3.3.25", {"start": v(0.75, -18.25) * mm, "end": v(0.75, -16.25) * mm});
            skLineSegment(sketch, "E14.6.3.25", {"start": v(0.75, -16.25) * mm, "end": v(2.75, -16.25) * mm});
            skLineSegment(sketch, "E14.9.3.25", {"start": v(0.75, -18.25) * mm, "end": v(2.75, -18.25) * mm});
            skLineSegment(sketch, "E14.0.3.26", {"start": v(2.75, -14.75) * mm, "end": v(2.75, -12.75) * mm});
            skLineSegment(sketch, "E14.3.3.26", {"start": v(0.75, -14.75) * mm, "end": v(0.75, -12.75) * mm});
            skLineSegment(sketch, "E14.6.3.26", {"start": v(0.75, -12.75) * mm, "end": v(2.75, -12.75) * mm});
            skLineSegment(sketch, "E14.9.3.26", {"start": v(0.75, -14.75) * mm, "end": v(2.75, -14.75) * mm});
            skLineSegment(sketch, "E14.0.3.27", {"start": v(2.75, -11.25) * mm, "end": v(2.75, -9.25) * mm});
            skLineSegment(sketch, "E14.3.3.27", {"start": v(0.75, -11.25) * mm, "end": v(0.75, -9.25) * mm});
            skLineSegment(sketch, "E14.6.3.27", {"start": v(0.75, -9.25) * mm, "end": v(2.75, -9.25) * mm});
            skLineSegment(sketch, "E14.9.3.27", {"start": v(0.75, -11.25) * mm, "end": v(2.75, -11.25) * mm});
            skLineSegment(sketch, "E14.0.3.28", {"start": v(2.75, -7.75) * mm, "end": v(2.75, -5.75) * mm});
            skLineSegment(sketch, "E14.3.3.28", {"start": v(0.75, -7.75) * mm, "end": v(0.75, -5.75) * mm});
            skLineSegment(sketch, "E14.6.3.28", {"start": v(0.75, -5.75) * mm, "end": v(2.75, -5.75) * mm});
            skLineSegment(sketch, "E14.9.3.28", {"start": v(0.75, -7.75) * mm, "end": v(2.75, -7.75) * mm});
            skLineSegment(sketch, "E14.0.3.29", {"start": v(2.75, -4.25) * mm, "end": v(2.75, -2.25) * mm});
            skLineSegment(sketch, "E14.3.3.29", {"start": v(0.75, -4.25) * mm, "end": v(0.75, -2.25) * mm});
            skLineSegment(sketch, "E14.6.3.29", {"start": v(0.75, -2.25) * mm, "end": v(2.75, -2.25) * mm});
            skLineSegment(sketch, "E14.9.3.29", {"start": v(0.75, -4.25) * mm, "end": v(2.75, -4.25) * mm});
            skLineSegment(sketch, "E14.0.4.25", {"start": v(6.25, -18.25) * mm, "end": v(6.25, -16.25) * mm});
            skLineSegment(sketch, "E14.3.4.25", {"start": v(4.25, -18.25) * mm, "end": v(4.25, -16.25) * mm});
            skLineSegment(sketch, "E14.6.4.25", {"start": v(4.25, -16.25) * mm, "end": v(6.25, -16.25) * mm});
            skLineSegment(sketch, "E14.9.4.25", {"start": v(4.25, -18.25) * mm, "end": v(6.25, -18.25) * mm});
            skLineSegment(sketch, "E14.0.4.26", {"start": v(6.25, -14.75) * mm, "end": v(6.25, -12.75) * mm});
            skLineSegment(sketch, "E14.3.4.26", {"start": v(4.25, -14.75) * mm, "end": v(4.25, -12.75) * mm});
            skLineSegment(sketch, "E14.6.4.26", {"start": v(4.25, -12.75) * mm, "end": v(6.25, -12.75) * mm});
            skLineSegment(sketch, "E14.9.4.26", {"start": v(4.25, -14.75) * mm, "end": v(6.25, -14.75) * mm});
            skLineSegment(sketch, "E14.0.4.27", {"start": v(6.25, -11.25) * mm, "end": v(6.25, -9.25) * mm});
            skLineSegment(sketch, "E14.3.4.27", {"start": v(4.25, -11.25) * mm, "end": v(4.25, -9.25) * mm});
            skLineSegment(sketch, "E14.6.4.27", {"start": v(4.25, -9.25) * mm, "end": v(6.25, -9.25) * mm});
            skLineSegment(sketch, "E14.9.4.27", {"start": v(4.25, -11.25) * mm, "end": v(6.25, -11.25) * mm});
            skLineSegment(sketch, "E14.0.4.28", {"start": v(6.25, -7.75) * mm, "end": v(6.25, -5.75) * mm});
            skLineSegment(sketch, "E14.3.4.28", {"start": v(4.25, -7.75) * mm, "end": v(4.25, -5.75) * mm});
            skLineSegment(sketch, "E14.6.4.28", {"start": v(4.25, -5.75) * mm, "end": v(6.25, -5.75) * mm});
            skLineSegment(sketch, "E14.9.4.28", {"start": v(4.25, -7.75) * mm, "end": v(6.25, -7.75) * mm});
            skLineSegment(sketch, "E14.0.4.29", {"start": v(6.25, -4.25) * mm, "end": v(6.25, -2.25) * mm});
            skLineSegment(sketch, "E14.3.4.29", {"start": v(4.25, -4.25) * mm, "end": v(4.25, -2.25) * mm});
            skLineSegment(sketch, "E14.6.4.29", {"start": v(4.25, -2.25) * mm, "end": v(6.25, -2.25) * mm});
            skLineSegment(sketch, "E14.9.4.29", {"start": v(4.25, -4.25) * mm, "end": v(6.25, -4.25) * mm});
            skLineSegment(sketch, "E14.0.5.25", {"start": v(9.75, -18.25) * mm, "end": v(9.75, -16.25) * mm});
            skLineSegment(sketch, "E14.3.5.25", {"start": v(7.75, -18.25) * mm, "end": v(7.75, -16.25) * mm});
            skLineSegment(sketch, "E14.6.5.25", {"start": v(7.75, -16.25) * mm, "end": v(9.75, -16.25) * mm});
            skLineSegment(sketch, "E14.9.5.25", {"start": v(7.75, -18.25) * mm, "end": v(9.75, -18.25) * mm});
            skLineSegment(sketch, "E14.0.5.26", {"start": v(9.75, -14.75) * mm, "end": v(9.75, -12.75) * mm});
            skLineSegment(sketch, "E14.3.5.26", {"start": v(7.75, -14.75) * mm, "end": v(7.75, -12.75) * mm});
            skLineSegment(sketch, "E14.6.5.26", {"start": v(7.75, -12.75) * mm, "end": v(9.75, -12.75) * mm});
            skLineSegment(sketch, "E14.9.5.26", {"start": v(7.75, -14.75) * mm, "end": v(9.75, -14.75) * mm});
            skLineSegment(sketch, "E14.0.5.27", {"start": v(9.75, -11.25) * mm, "end": v(9.75, -9.25) * mm});
            skLineSegment(sketch, "E14.3.5.27", {"start": v(7.75, -11.25) * mm, "end": v(7.75, -9.25) * mm});
            skLineSegment(sketch, "E14.6.5.27", {"start": v(7.75, -9.25) * mm, "end": v(9.75, -9.25) * mm});
            skLineSegment(sketch, "E14.9.5.27", {"start": v(7.75, -11.25) * mm, "end": v(9.75, -11.25) * mm});
            skLineSegment(sketch, "E14.0.5.28", {"start": v(9.75, -7.75) * mm, "end": v(9.75, -5.75) * mm});
            skLineSegment(sketch, "E14.3.5.28", {"start": v(7.75, -7.75) * mm, "end": v(7.75, -5.75) * mm});
            skLineSegment(sketch, "E14.6.5.28", {"start": v(7.75, -5.75) * mm, "end": v(9.75, -5.75) * mm});
            skLineSegment(sketch, "E14.9.5.28", {"start": v(7.75, -7.75) * mm, "end": v(9.75, -7.75) * mm});
            skLineSegment(sketch, "E14.0.5.29", {"start": v(9.75, -4.25) * mm, "end": v(9.75, -2.25) * mm});
            skLineSegment(sketch, "E14.3.5.29", {"start": v(7.75, -4.25) * mm, "end": v(7.75, -2.25) * mm});
            skLineSegment(sketch, "E14.6.5.29", {"start": v(7.75, -2.25) * mm, "end": v(9.75, -2.25) * mm});
            skLineSegment(sketch, "E14.9.5.29", {"start": v(7.75, -4.25) * mm, "end": v(9.75, -4.25) * mm});
            skSolve(sketch);
        }
        {
            var Q0;
            Q0 = qSketchRegion(id + "F2", true);
            extrude(context, id + "F3", {"entities" : qUnion([Q0]), "operationType" : NewBodyOperationType.REMOVE, "endBound" : BoundingType.UP_TO_NEXT, "oppositeDirection" : true, "depth" : 25 * mm, "hasDraft" : true, "draftAngle" : 12 * degree});
        }
        {
            var Q0;
            Q0=makeQuery(id+"F1.opExtrude","SWEPT_EDGE",EDGE,{"disambiguationData":[OSD([sQuery(id+"F0.wireOp",EDGE,"E9"),sQuery(id+"F0.wireOp",EDGE,"E11")])]});
            var Q1;
            Q1=makeQuery(id+"F1.opExtrude","SWEPT_EDGE",EDGE,{"disambiguationData":[OSD([sQuery(id+"F0.wireOp",EDGE,"E9"),sQuery(id+"F0.wireOp",EDGE,"E10")])]});
            var Q2;
            Q2=makeQuery(id+"F1.opExtrude","SWEPT_EDGE",EDGE,{"disambiguationData":[OSD([sQuery(id+"F0.wireOp",EDGE,"E6.trimOffspring"),sQuery(id+"F0.wireOp",EDGE,"E11")])]});
            var Q3;
            Q3=makeQuery(id+"F1.opExtrude","SWEPT_EDGE",EDGE,{"disambiguationData":[OSD([sQuery(id+"F0.wireOp",EDGE,"E5"),sQuery(id+"F0.wireOp",EDGE,"E10")])]});
            fillet(context, id + "F4", {"entities" : qUnion([Q0, Q1, Q2, Q3]), "radius" : 1.5 * mm, "tangentPropagation" : true, "allowEdgeOverflow" : false});
        }
        {
            var Q0;
            Q0=makeQuery(id+"F1.opExtrude","CAP_FACE",FACE,{"disambiguationData":[OSD([sQuery(id+"F0.wireOp",EDGE,"E0.bottom"),sQuery(id+"F0.wireOp",EDGE,"E0.left"),sQuery(id+"F0.wireOp",EDGE,"E0.right"),sQuery(id+"F0.wireOp",EDGE,"E3"),sQuery(id+"F0.wireOp",EDGE,"E4"),sQuery(id+"F0.wireOp",EDGE,"E5"),sQuery(id+"F0.wireOp",EDGE,"E6.trimOffspring"),sQuery(id+"F0.wireOp",EDGE,"E7.trimOffspring"),sQuery(id+"F0.wireOp",EDGE,"E8"),sQuery(id+"F0.wireOp",EDGE,"E9"),sQuery(id+"F0.wireOp",EDGE,"E10"),sQuery(id+"F0.wireOp",EDGE,"E11")])],"isStart":false});
            var sketch = newSketch(context, id + "F5", { "sketchPlane" : qUnion([Q0])});
            skLineSegment(sketch, "E15.bottom", {"start": v(-12, -5.1) * mm, "end": v(12, -5.1) * mm});
            skLineSegment(sketch, "E15.top", {"start": v(-10.5, 6.9) * mm, "end": v(10.5, 6.9) * mm});
            skLineSegment(sketch, "E15.left", {"start": v(-12, -5.1) * mm, "end": v(-12, 5.4) * mm});
            skLineSegment(sketch, "E15.right", {"start": v(12, -5.1) * mm, "end": v(12, 5.4) * mm});
            skPoint(sketch, "E16.visualSharp", {"position": v(12, 6.9) * mm});
            skArc(sketch, "E16.filletArc", {"start": v(12, 5.4) * mm, "mid": v(11.56, 6.46) * mm, "end": v(10.5, 6.9) * mm});
            skPoint(sketch, "E17.visualSharp", {"position": v(-12, 6.9) * mm});
            skArc(sketch, "E17.filletArc", {"start": v(-10.5, 6.9) * mm, "mid": v(-11.56, 6.46) * mm, "end": v(-12, 5.4) * mm});
            skSolve(sketch);
        }
        {
            var Q0;
            Q0 = qSketchRegion(id + "F5", true);
            extrude(context, id + "F6", {"entities" : qUnion([Q0]), "depth" : 2 * mm});
        }
    });
